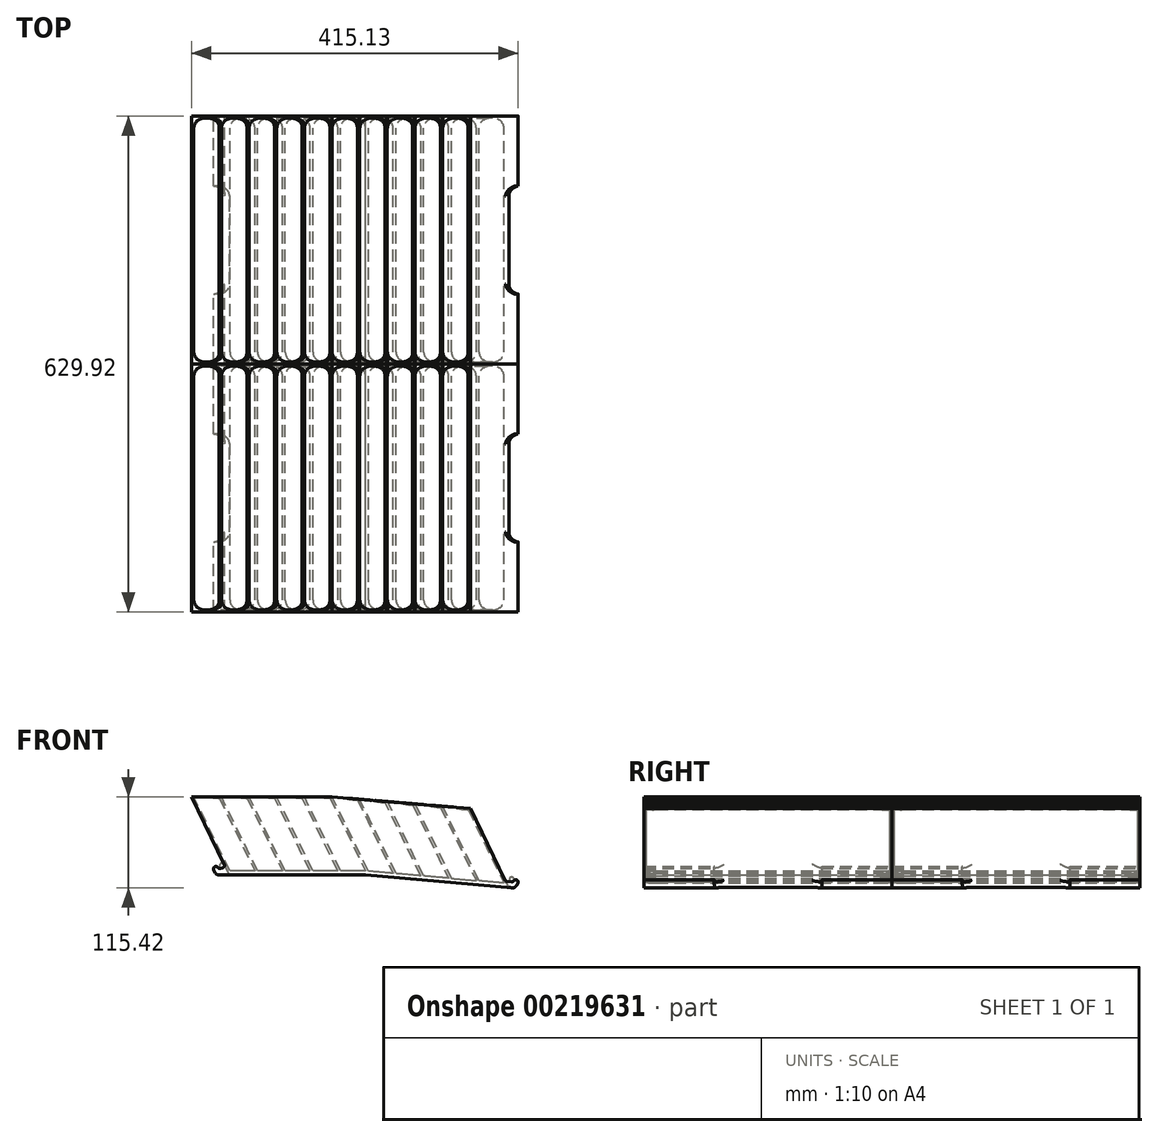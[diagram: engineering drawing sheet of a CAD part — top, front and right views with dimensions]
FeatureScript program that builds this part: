
annotation { "Feature Type Name" : "Feature", "Feature Type Description" : "" }
export const myFeature = defineFeature(function(context is Context, id is Id, definition is map)
    precondition{}
    {
        {
            var Q0;
            Q0=qCreatedBy(makeId("Front.planeOp"),FACE);
            var sketch = newSketch(context, id + "F0", { "sketchPlane" : qUnion([Q0])});
            skLineSegment(sketch, "E0", {"start": v(0, 0) * mm, "end": v(189.48, 0) * mm});
            skLineSegment(sketch, "E1", {"start": v(189.48, 0) * mm, "end": v(379.26, -16.6) * mm});
            skLineSegment(sketch, "E2", {"start": v(367.73, -8.25) * mm, "end": v(332.9, 63.16) * mm});
            skLineSegment(sketch, "E3", {"start": v(332.9, 63.16) * mm, "end": v(330.16, 61.83) * mm, "construction": true});
            skLineSegment(sketch, "E4", {"start": v(330.16, 61.83) * mm, "end": v(365.33, -10.29) * mm});
            skLineSegment(sketch, "E5", {"start": v(11.64, 10.16) * mm, "end": v(-21.71, 78.55) * mm});
            skLineSegment(sketch, "E6", {"start": v(-21.71, 78.55) * mm, "end": v(-18.66, 78.55) * mm});
            skLineSegment(sketch, "E7", {"start": v(-18.66, 78.55) * mm, "end": v(17.17, 5.08) * mm});
            skLineSegment(sketch, "E8", {"start": v(17.17, 5.08) * mm, "end": v(48.92, 5.08) * mm});
            skLineSegment(sketch, "E9", {"start": v(48.92, 5.08) * mm, "end": v(13.74, 77.21) * mm});
            skLineSegment(sketch, "E10", {"start": v(13.74, 77.21) * mm, "end": v(16.48, 78.55) * mm});
            skLineSegment(sketch, "E11", {"start": v(16.48, 78.55) * mm, "end": v(52.31, 5.08) * mm});
            skLineSegment(sketch, "E12", {"start": v(52.31, 5.08) * mm, "end": v(84.06, 5.08) * mm});
            skLineSegment(sketch, "E13", {"start": v(84.06, 5.08) * mm, "end": v(48.88, 77.21) * mm});
            skLineSegment(sketch, "E14", {"start": v(48.88, 77.21) * mm, "end": v(51.62, 78.55) * mm, "construction": true});
            skLineSegment(sketch, "E15", {"start": v(51.62, 78.55) * mm, "end": v(87.45, 5.08) * mm});
            skLineSegment(sketch, "E16", {"start": v(87.45, 5.08) * mm, "end": v(119.2, 5.08) * mm});
            skLineSegment(sketch, "E17", {"start": v(119.2, 5.08) * mm, "end": v(84.02, 77.21) * mm});
            skLineSegment(sketch, "E18", {"start": v(86.76, 78.55) * mm, "end": v(122.6, 5.08) * mm});
            skLineSegment(sketch, "E19", {"start": v(122.6, 5.08) * mm, "end": v(154.34, 5.08) * mm});
            skLineSegment(sketch, "E20", {"start": v(154.34, 5.08) * mm, "end": v(119.16, 77.21) * mm});
            skLineSegment(sketch, "E21", {"start": v(119.16, 77.21) * mm, "end": v(121.9, 78.55) * mm, "construction": true});
            skLineSegment(sketch, "E22", {"start": v(121.9, 78.55) * mm, "end": v(157.73, 5.08) * mm});
            skLineSegment(sketch, "E23", {"start": v(157.73, 5.08) * mm, "end": v(189.48, 5.08) * mm});
            skLineSegment(sketch, "E24", {"start": v(189.48, 0) * mm, "end": v(189.48, 5.08) * mm, "construction": true});
            skLineSegment(sketch, "E25", {"start": v(189.48, 5.08) * mm, "end": v(154.3, 77.21) * mm});
            skLineSegment(sketch, "E26", {"start": v(154.3, 77.21) * mm, "end": v(157.04, 78.55) * mm, "construction": true});
            skLineSegment(sketch, "E27", {"start": v(157.04, 78.55) * mm, "end": v(193.02, 4.8) * mm});
            skLineSegment(sketch, "E28", {"start": v(193.02, 4.8) * mm, "end": v(224.65, 2.02) * mm});
            skLineSegment(sketch, "E29", {"start": v(224.65, 2.02) * mm, "end": v(189.47, 74.14) * mm});
            skLineSegment(sketch, "E30", {"start": v(189.47, 74.14) * mm, "end": v(192.21, 75.47) * mm, "construction": true});
            skLineSegment(sketch, "E31", {"start": v(192.21, 75.47) * mm, "end": v(228.19, 1.71) * mm});
            skLineSegment(sketch, "E32", {"start": v(224.65, 2.02) * mm, "end": v(228.19, 1.71) * mm, "construction": true});
            skLineSegment(sketch, "E33", {"start": v(228.19, 1.71) * mm, "end": v(259.82, -1.05) * mm});
            skLineSegment(sketch, "E34", {"start": v(259.82, -1.05) * mm, "end": v(224.65, 71.06) * mm});
            skLineSegment(sketch, "E35", {"start": v(224.65, 71.06) * mm, "end": v(227.39, 72.4) * mm, "construction": true});
            skLineSegment(sketch, "E36", {"start": v(227.39, 72.4) * mm, "end": v(263.36, -1.36) * mm});
            skLineSegment(sketch, "E37", {"start": v(263.36, -1.36) * mm, "end": v(294.99, -4.13) * mm});
            skLineSegment(sketch, "E38", {"start": v(294.99, -4.13) * mm, "end": v(259.82, 67.98) * mm});
            skLineSegment(sketch, "E39", {"start": v(259.82, 67.98) * mm, "end": v(262.56, 69.32) * mm, "construction": true});
            skLineSegment(sketch, "E40", {"start": v(262.56, 69.32) * mm, "end": v(298.53, -4.44) * mm});
            skLineSegment(sketch, "E41", {"start": v(298.53, -4.44) * mm, "end": v(330.16, -7.2) * mm});
            skLineSegment(sketch, "E42", {"start": v(330.16, -7.2) * mm, "end": v(294.99, 64.9) * mm});
            skLineSegment(sketch, "E43", {"start": v(294.99, 64.9) * mm, "end": v(297.73, 66.24) * mm, "construction": true});
            skLineSegment(sketch, "E44", {"start": v(297.73, 66.24) * mm, "end": v(333.7, -7.52) * mm});
            skLineSegment(sketch, "E45", {"start": v(333.7, -7.52) * mm, "end": v(365.33, -10.29) * mm});
            skLineSegment(sketch, "E46", {"start": v(-18.66, 78.55) * mm, "end": v(157.04, 78.55) * mm, "construction": true});
            skLineSegment(sketch, "E47", {"start": v(157.04, 78.55) * mm, "end": v(332.9, 63.16) * mm, "construction": true});
            skLineSegment(sketch, "E48", {"start": v(84.02, 77.21) * mm, "end": v(86.76, 78.55) * mm, "construction": true});
            skLineSegment(sketch, "E49", {"start": v(367.73, -8.25) * mm, "end": v(376.94, -9.06) * mm});
            skLineSegment(sketch, "E50", {"start": v(379.26, -16.6) * mm, "end": v(383.77, -9.65) * mm});
            skArc(sketch, "E51", {"start": v(383.77, -9.65) * mm, "mid": v(380.63, -6.27) * mm, "end": v(376.94, -9.06) * mm});
            skLineSegment(sketch, "E52", {"start": v(376.94, -9.06) * mm, "end": v(383.77, -9.65) * mm, "construction": true});
            skLineSegment(sketch, "E53", {"start": v(0, 0) * mm, "end": v(-4.05, 7.62) * mm});
            skLineSegment(sketch, "E54", {"start": v(11.64, 10.16) * mm, "end": v(2.8, 7.62) * mm});
            skArc(sketch, "E55", {"start": v(2.8, 7.62) * mm, "mid": v(-0.62, 10.67) * mm, "end": v(-4.05, 7.62) * mm});
            skLineSegment(sketch, "E56", {"start": v(-4.05, 7.62) * mm, "end": v(2.8, 7.62) * mm, "construction": true});
            skLineSegment(sketch, "E57", {"start": v(-21.71, 78.55) * mm, "end": v(-31.72, 99.06) * mm});
            skLineSegment(sketch, "E58", {"start": v(-31.72, 99.06) * mm, "end": v(-28.67, 99.06) * mm});
            skLineSegment(sketch, "E59", {"start": v(-28.67, 99.06) * mm, "end": v(-18.66, 78.55) * mm});
            skLineSegment(sketch, "E60", {"start": v(13.74, 77.21) * mm, "end": v(3.73, 97.72) * mm});
            skLineSegment(sketch, "E61", {"start": v(3.73, 97.72) * mm, "end": v(6.47, 99.06) * mm});
            skLineSegment(sketch, "E62", {"start": v(6.47, 99.06) * mm, "end": v(16.48, 78.55) * mm});
            skLineSegment(sketch, "E63", {"start": v(48.88, 77.21) * mm, "end": v(38.87, 97.72) * mm});
            skLineSegment(sketch, "E64", {"start": v(38.87, 97.72) * mm, "end": v(41.61, 99.06) * mm});
            skLineSegment(sketch, "E65", {"start": v(41.61, 99.06) * mm, "end": v(51.62, 78.55) * mm});
            skLineSegment(sketch, "E66", {"start": v(109.16, 97.72) * mm, "end": v(111.9, 99.06) * mm});
            skLineSegment(sketch, "E67", {"start": v(259.82, 67.98) * mm, "end": v(249.49, 89.16) * mm});
            skLineSegment(sketch, "E68", {"start": v(249.49, 89.16) * mm, "end": v(252.23, 90.5) * mm});
            skLineSegment(sketch, "E69", {"start": v(252.23, 90.5) * mm, "end": v(262.56, 69.32) * mm});
            skLineSegment(sketch, "E70", {"start": v(330.16, 61.83) * mm, "end": v(319.83, 83) * mm});
            skLineSegment(sketch, "E71", {"start": v(319.83, 83) * mm, "end": v(322.57, 84.34) * mm});
            skLineSegment(sketch, "E72", {"start": v(322.57, 84.34) * mm, "end": v(332.9, 63.16) * mm});
            skLineSegment(sketch, "E73", {"start": v(154.3, 77.21) * mm, "end": v(144.3, 97.72) * mm});
            skLineSegment(sketch, "E74", {"start": v(294.99, 64.9) * mm, "end": v(284.66, 86.08) * mm});
            skLineSegment(sketch, "E75", {"start": v(189.47, 74.14) * mm, "end": v(179.15, 95.31) * mm});
            skLineSegment(sketch, "E76", {"start": v(-28.67, 99.06) * mm, "end": v(154.3, 99.06) * mm, "construction": true});
            skLineSegment(sketch, "E77", {"start": v(322.57, 84.34) * mm, "end": v(154.3, 99.06) * mm, "construction": true});
            skLineSegment(sketch, "E78", {"start": v(86.76, 78.55) * mm, "end": v(76.76, 99.06) * mm});
            skLineSegment(sketch, "E79", {"start": v(76.76, 99.06) * mm, "end": v(74.02, 97.72) * mm});
            skLineSegment(sketch, "E80", {"start": v(74.02, 97.72) * mm, "end": v(84.02, 77.21) * mm});
            skLineSegment(sketch, "E81", {"start": v(109.16, 97.72) * mm, "end": v(119.16, 77.21) * mm});
            skLineSegment(sketch, "E82", {"start": v(111.9, 99.06) * mm, "end": v(121.9, 78.55) * mm});
            skLineSegment(sketch, "E83", {"start": v(157.04, 78.55) * mm, "end": v(147.04, 99.06) * mm});
            skLineSegment(sketch, "E84", {"start": v(147.04, 99.06) * mm, "end": v(144.3, 97.72) * mm});
            skLineSegment(sketch, "E85", {"start": v(192.21, 75.47) * mm, "end": v(181.89, 96.65) * mm});
            skLineSegment(sketch, "E86", {"start": v(181.89, 96.65) * mm, "end": v(179.15, 95.31) * mm});
            skLineSegment(sketch, "E87", {"start": v(227.39, 72.4) * mm, "end": v(217.06, 93.57) * mm});
            skLineSegment(sketch, "E88", {"start": v(217.06, 93.57) * mm, "end": v(214.32, 92.23) * mm});
            skLineSegment(sketch, "E89", {"start": v(214.32, 92.23) * mm, "end": v(224.65, 71.06) * mm});
            skLineSegment(sketch, "E90", {"start": v(297.73, 66.24) * mm, "end": v(287.4, 87.42) * mm});
            skLineSegment(sketch, "E91", {"start": v(287.4, 87.42) * mm, "end": v(284.66, 86.08) * mm});
            skSolve(sketch);
        }
        {
            var Q0;
            Q0=qSketchRegion(id+"F0",true);
            extrude(context, id + "F1", {"entities" : qUnion([Q0]), "endBound" : BoundingType.SYMMETRIC, "depth" : 314.96 * mm});
        }
        {
            var Q0;
            Q0=makeQuery(id+"F1.opExtrude","SWEPT_EDGE",EDGE,{"disambiguationData":[OSD([sQuery(id+"F0.wireOp",EDGE,"E5"),sQuery(id+"F0.wireOp",EDGE,"E54")])]});
            var Q1;
            Q1=makeQuery(id+"F1.opExtrude","SWEPT_EDGE",EDGE,{"disambiguationData":[OSD([sQuery(id+"F0.wireOp",EDGE,"E54"),sQuery(id+"F0.wireOp",EDGE,"E55")])]});
            var Q2;
            Q2=makeQuery(id+"F1.opExtrude","SWEPT_EDGE",EDGE,{"disambiguationData":[OSD([sQuery(id+"F0.wireOp",EDGE,"E2"),sQuery(id+"F0.wireOp",EDGE,"E49")])]});
            var Q3;
            Q3=makeQuery(id+"F1.opExtrude","SWEPT_EDGE",EDGE,{"disambiguationData":[OSD([sQuery(id+"F0.wireOp",EDGE,"E49"),sQuery(id+"F0.wireOp",EDGE,"E51")])]});
            var Q4;
            Q4=makeQuery(id+"F1.opExtrude","SWEPT_EDGE",EDGE,{"disambiguationData":[OSD([sQuery(id+"F0.wireOp",EDGE,"E50"),sQuery(id+"F0.wireOp",EDGE,"E51")])]});
            var Q5;
            Q5=makeQuery(id+"F1.opExtrude","SWEPT_EDGE",EDGE,{"disambiguationData":[OSD([sQuery(id+"F0.wireOp",EDGE,"E53"),sQuery(id+"F0.wireOp",EDGE,"E55")])]});
            fillet(context, id + "F2", {"entities" : qUnion([Q0, Q1, Q2, Q3, Q4, Q5]), "radius" : 3.05 * mm, "tangentPropagation" : true, "allowEdgeOverflow" : false});
        }
        {
            var Q0;
            Q0=makeQuery(id+"F1.opExtrude","SWEPT_EDGE",EDGE,{"disambiguationData":[OSD([sQuery(id+"F0.wireOp",EDGE,"E0"),sQuery(id+"F0.wireOp",EDGE,"E53")])]});
            var Q1;
            Q1=makeQuery(id+"F1.opExtrude","SWEPT_EDGE",EDGE,{"disambiguationData":[OSD([sQuery(id+"F0.wireOp",EDGE,"E1"),sQuery(id+"F0.wireOp",EDGE,"E50")])]});
            fillet(context, id + "F3", {"entities" : qUnion([Q0, Q1]), "radius" : 5.08 * mm, "tangentPropagation" : true, "allowEdgeOverflow" : false});
        }
        {
            var Q0;
            Q0=makeQuery(id+"F1.opExtrude","CAP_FACE",FACE,{"disambiguationData":[OSD([sQuery(id+"F0.wireOp",EDGE,"E0"),sQuery(id+"F0.wireOp",EDGE,"E1"),sQuery(id+"F0.wireOp",EDGE,"E2"),sQuery(id+"F0.wireOp",EDGE,"E3"),sQuery(id+"F0.wireOp",EDGE,"E4"),sQuery(id+"F0.wireOp",EDGE,"E5"),sQuery(id+"F0.wireOp",EDGE,"E6"),sQuery(id+"F0.wireOp",EDGE,"E7"),sQuery(id+"F0.wireOp",EDGE,"E8"),sQuery(id+"F0.wireOp",EDGE,"E9"),sQuery(id+"F0.wireOp",EDGE,"E10"),sQuery(id+"F0.wireOp",EDGE,"E11"),sQuery(id+"F0.wireOp",EDGE,"E12"),sQuery(id+"F0.wireOp",EDGE,"E13"),sQuery(id+"F0.wireOp",EDGE,"E14"),sQuery(id+"F0.wireOp",EDGE,"E15"),sQuery(id+"F0.wireOp",EDGE,"E16"),sQuery(id+"F0.wireOp",EDGE,"E17"),sQuery(id+"F0.wireOp",EDGE,"E18"),sQuery(id+"F0.wireOp",EDGE,"E19"),sQuery(id+"F0.wireOp",EDGE,"E20"),sQuery(id+"F0.wireOp",EDGE,"E21"),sQuery(id+"F0.wireOp",EDGE,"E22"),sQuery(id+"F0.wireOp",EDGE,"E23"),sQuery(id+"F0.wireOp",EDGE,"E25"),sQuery(id+"F0.wireOp",EDGE,"E26"),sQuery(id+"F0.wireOp",EDGE,"E27"),sQuery(id+"F0.wireOp",EDGE,"E28"),sQuery(id+"F0.wireOp",EDGE,"E29"),sQuery(id+"F0.wireOp",EDGE,"E30"),sQuery(id+"F0.wireOp",EDGE,"E31"),sQuery(id+"F0.wireOp",EDGE,"E33"),sQuery(id+"F0.wireOp",EDGE,"E34"),sQuery(id+"F0.wireOp",EDGE,"E35"),sQuery(id+"F0.wireOp",EDGE,"E36"),sQuery(id+"F0.wireOp",EDGE,"E37"),sQuery(id+"F0.wireOp",EDGE,"E38"),sQuery(id+"F0.wireOp",EDGE,"E39"),sQuery(id+"F0.wireOp",EDGE,"E40"),sQuery(id+"F0.wireOp",EDGE,"E41"),sQuery(id+"F0.wireOp",EDGE,"E42"),sQuery(id+"F0.wireOp",EDGE,"E43"),sQuery(id+"F0.wireOp",EDGE,"E44"),sQuery(id+"F0.wireOp",EDGE,"E45"),sQuery(id+"F0.wireOp",EDGE,"E48"),sQuery(id+"F0.wireOp",EDGE,"E49"),sQuery(id+"F0.wireOp",EDGE,"E50"),sQuery(id+"F0.wireOp",EDGE,"E51"),sQuery(id+"F0.wireOp",EDGE,"E53"),sQuery(id+"F0.wireOp",EDGE,"E54"),sQuery(id+"F0.wireOp",EDGE,"E55")])],"isStart":false});
            var sketch = newSketch(context, id + "F4", { "sketchPlane" : qUnion([Q0])});
            skLineSegment(sketch, "E92.0", {"start": v(10.05, 13.42) * mm, "end": v(-31.72, 99.06) * mm});
            skArc(sketch, "E92.1", {"start": v(10.05, 13.42) * mm, "mid": v(10.1, 10.85) * mm, "end": v(8.15, 9.16) * mm});
            skLineSegment(sketch, "E92.2", {"start": v(8.15, 9.16) * mm, "end": v(5.3, 8.34) * mm});
            skArc(sketch, "E92.3", {"start": v(5.3, 8.34) * mm, "mid": v(3.53, 8.36) * mm, "end": v(2.08, 9.37) * mm});
            skArc(sketch, "E92.4", {"start": v(2.08, 9.37) * mm, "mid": v(0.97, 10.28) * mm, "end": v(-0.42, 10.66) * mm});
            skArc(sketch, "E92.5", {"start": v(-0.42, 10.66) * mm, "mid": v(-3.17, 9.26) * mm, "end": v(-3.3, 6.19) * mm});
            skLineSegment(sketch, "E92.6", {"start": v(-1.43, 2.7) * mm, "end": v(-3.3, 6.19) * mm});
            skArc(sketch, "E92.7", {"start": v(-1.43, 2.7) * mm, "mid": v(0.44, 0.73) * mm, "end": v(3.05, 0) * mm});
            skLineSegment(sketch, "E92.8", {"start": v(3.05, 0) * mm, "end": v(189.48, 0) * mm});
            skLineSegment(sketch, "E92.9", {"start": v(189.48, 0) * mm, "end": v(376.22, -16.34) * mm});
            skLineSegment(sketch, "E92.10", {"start": v(366.98, -6.7) * mm, "end": v(322.57, 84.34) * mm});
            skArc(sketch, "E92.11", {"start": v(369.45, -8.4) * mm, "mid": v(367.99, -7.88) * mm, "end": v(366.98, -6.7) * mm});
            skLineSegment(sketch, "E92.12", {"start": v(369.45, -8.4) * mm, "end": v(374.84, -8.87) * mm});
            skArc(sketch, "E92.13", {"start": v(377.56, -7.65) * mm, "mid": v(376.36, -8.62) * mm, "end": v(374.84, -8.87) * mm});
            skArc(sketch, "E92.14", {"start": v(380.66, -6.27) * mm, "mid": v(378.93, -6.55) * mm, "end": v(377.56, -7.65) * mm});
            skArc(sketch, "E92.15", {"start": v(382.92, -10.97) * mm, "mid": v(383.1, -7.98) * mm, "end": v(380.66, -6.27) * mm});
            skLineSegment(sketch, "E92.16", {"start": v(380.92, -14.04) * mm, "end": v(382.92, -10.97) * mm});
            skArc(sketch, "E92.17", {"start": v(376.22, -16.34) * mm, "mid": v(378.89, -15.84) * mm, "end": v(380.92, -14.04) * mm});
            skLineSegment(sketch, "E93", {"start": v(322.57, 84.34) * mm, "end": v(147.04, 99.06) * mm});
            skLineSegment(sketch, "E94", {"start": v(147.04, 99.06) * mm, "end": v(-31.72, 99.06) * mm});
            skSolve(sketch);
        }
        {
            var Q0;
            Q0=qSketchRegion(id+"F4",true);
            extrude(context, id + "F5", {"entities" : qUnion([Q0]), "oppositeDirection" : true, "depth" : 2.54 * mm});
        }
        {
            var Q0;
            Q0=makeQuery(id+"F5.opExtrude","SWEPT_BODY",BODY,{"disambiguationData":[OSD([sQuery(id+"F4.wireOp",EDGE,"E92.0"),sQuery(id+"F4.wireOp",EDGE,"E92.1"),sQuery(id+"F4.wireOp",EDGE,"E92.2"),sQuery(id+"F4.wireOp",EDGE,"E92.3"),sQuery(id+"F4.wireOp",EDGE,"E92.4"),sQuery(id+"F4.wireOp",EDGE,"E92.5"),sQuery(id+"F4.wireOp",EDGE,"E92.6"),sQuery(id+"F4.wireOp",EDGE,"E92.7"),sQuery(id+"F4.wireOp",EDGE,"E92.8"),sQuery(id+"F4.wireOp",EDGE,"E92.9"),sQuery(id+"F4.wireOp",EDGE,"E92.10"),sQuery(id+"F4.wireOp",EDGE,"E92.11"),sQuery(id+"F4.wireOp",EDGE,"E92.12"),sQuery(id+"F4.wireOp",EDGE,"E92.13"),sQuery(id+"F4.wireOp",EDGE,"E92.14"),sQuery(id+"F4.wireOp",EDGE,"E92.15"),sQuery(id+"F4.wireOp",EDGE,"E92.16"),sQuery(id+"F4.wireOp",EDGE,"E92.17"),sQuery(id+"F4.wireOp",EDGE,"E93"),sQuery(id+"F4.wireOp",EDGE,"E94")])]});
            var Q1;
            Q1=qCreatedBy(makeId("Front.planeOp"),FACE);
            mirror(context, id + "F6", {"operationType" : NewBodyOperationType.ADD, "entities" : qUnion([Q0]), "mirrorPlane" : qUnion([Q1])});
        }
        {
            var Q0;
            Q0=makeQuery(id+"F1.opExtrude","SWEPT_FACE",FACE,{"disambiguationData":[OSD([sQuery(id+"F0.wireOp",EDGE,"E61")])]});
            var sketch = newSketch(context, id + "F7", { "sketchPlane" : qUnion([Q0])});
            skLineSegment(sketch, "E95.bottom", {"start": v(14.92, -68.58) * mm, "end": v(-14.92, -68.58) * mm});
            skLineSegment(sketch, "E95.top", {"start": v(14.92, 68.58) * mm, "end": v(-14.92, 68.58) * mm});
            skLineSegment(sketch, "E95.left", {"start": v(14.92, -68.58) * mm, "end": v(14.92, 68.58) * mm});
            skLineSegment(sketch, "E95.right", {"start": v(-14.92, -68.58) * mm, "end": v(-14.92, 68.58) * mm});
            skPoint(sketch, "E95.middle", {"position": v(0, 0) * mm});
            skSolve(sketch);
        }
        {
            var Q0;
            Q0=qSketchRegion(id+"F7",true);
            extrude(context, id + "F8", {"entities" : qUnion([Q0]), "operationType" : NewBodyOperationType.REMOVE, "oppositeDirection" : true, "depth" : 144.78 * mm});
        }
        {
            var Q0;
            Q0=makeQuery(id+"F1.opExtrude","SWEPT_FACE",FACE,{"disambiguationData":[OSD([sQuery(id+"F0.wireOp",EDGE,"E61")])]});
            var sketch = newSketch(context, id + "F9", { "sketchPlane" : qUnion([Q0])});
            skLineSegment(sketch, "E96.bottom", {"start": v(326.9, -68.58) * mm, "end": v(466.95, -68.58) * mm});
            skLineSegment(sketch, "E96.top", {"start": v(326.9, 68.58) * mm, "end": v(466.95, 68.58) * mm});
            skLineSegment(sketch, "E96.left", {"start": v(326.9, -68.58) * mm, "end": v(326.9, 68.58) * mm});
            skLineSegment(sketch, "E96.right", {"start": v(466.95, -68.58) * mm, "end": v(466.95, 68.58) * mm});
            skPoint(sketch, "E96.middle", {"position": v(396.93, 0) * mm});
            skSolve(sketch);
        }
        {
            var Q0;
            Q0=qSketchRegion(id+"F9",true);
            extrude(context, id + "F10", {"entities" : qUnion([Q0]), "operationType" : NewBodyOperationType.REMOVE, "oppositeDirection" : true, "depth" : 293.12 * mm});
        }
        {
            var Q0;
            Q0=makeQuery(id+"F10.boolean.opBoolean","COPY",EDGE,{"derivedFrom":makeQuery(id+"F10.opExtrude","SWEPT_EDGE",EDGE,{"disambiguationData":[OSD([sQuery(id+"F9.wireOp",EDGE,"E96.bottom"),sQuery(id+"F9.wireOp",EDGE,"E96.left")])]})});
            var Q1;
            Q1=makeQuery(id+"F10.boolean.opBoolean","COPY",EDGE,{"derivedFrom":makeQuery(id+"F10.opExtrude","SWEPT_EDGE",EDGE,{"disambiguationData":[OSD([sQuery(id+"F9.wireOp",EDGE,"E96.top"),sQuery(id+"F9.wireOp",EDGE,"E96.left")])]})});
            var Q2;
            Q2=makeQuery(id+"F8.boolean.opBoolean","COPY",EDGE,{"derivedFrom":makeQuery(id+"F8.opExtrude","SWEPT_EDGE",EDGE,{"disambiguationData":[OSD([sQuery(id+"F7.wireOp",EDGE,"E95.top"),sQuery(id+"F7.wireOp",EDGE,"E95.left")])]})});
            var Q3;
            Q3=makeQuery(id+"F8.boolean.opBoolean","COPY",EDGE,{"derivedFrom":makeQuery(id+"F8.opExtrude","SWEPT_EDGE",EDGE,{"disambiguationData":[OSD([sQuery(id+"F7.wireOp",EDGE,"E95.bottom"),sQuery(id+"F7.wireOp",EDGE,"E95.left")])]})});
            fillet(context, id + "F11", {"entities" : qUnion([Q0, Q1, Q2, Q3]), "radius" : 12.7 * mm, "tangentPropagation" : true, "allowEdgeOverflow" : false});
        }
        {
            var Q0;
            Q0=makeQuery(id+"F6.boolean.opBoolean","INTERSECT",EDGE,{"derivedFrom":[makeQuery(id+"F1.opExtrude","SWEPT_FACE",FACE,{"disambiguationData":[OSD([sQuery(id+"F0.wireOp",EDGE,"E29"),sQuery(id+"F0.wireOp",EDGE,"E75")])]}),makeQuery(id+"F5.opExtrude","CAP_FACE",FACE,{"disambiguationData":[OSD([sQuery(id+"F4.wireOp",EDGE,"E92.0"),sQuery(id+"F4.wireOp",EDGE,"E92.1"),sQuery(id+"F4.wireOp",EDGE,"E92.2"),sQuery(id+"F4.wireOp",EDGE,"E92.3"),sQuery(id+"F4.wireOp",EDGE,"E92.4"),sQuery(id+"F4.wireOp",EDGE,"E92.5"),sQuery(id+"F4.wireOp",EDGE,"E92.6"),sQuery(id+"F4.wireOp",EDGE,"E92.7"),sQuery(id+"F4.wireOp",EDGE,"E92.8"),sQuery(id+"F4.wireOp",EDGE,"E92.9"),sQuery(id+"F4.wireOp",EDGE,"E92.10"),sQuery(id+"F4.wireOp",EDGE,"E92.11"),sQuery(id+"F4.wireOp",EDGE,"E92.12"),sQuery(id+"F4.wireOp",EDGE,"E92.13"),sQuery(id+"F4.wireOp",EDGE,"E92.14"),sQuery(id+"F4.wireOp",EDGE,"E92.15"),sQuery(id+"F4.wireOp",EDGE,"E92.16"),sQuery(id+"F4.wireOp",EDGE,"E92.17"),sQuery(id+"F4.wireOp",EDGE,"E93"),sQuery(id+"F4.wireOp",EDGE,"E94")])],"isStart":false})]});
            var Q1;
            Q1=makeQuery(id+"F6.boolean.opBoolean","INTERSECT",EDGE,{"derivedFrom":[makeQuery(id+"F1.opExtrude","SWEPT_FACE",FACE,{"disambiguationData":[OSD([sQuery(id+"F0.wireOp",EDGE,"E27"),sQuery(id+"F0.wireOp",EDGE,"E83")])]}),makeQuery(id+"F5.opExtrude","CAP_FACE",FACE,{"disambiguationData":[OSD([sQuery(id+"F4.wireOp",EDGE,"E92.0"),sQuery(id+"F4.wireOp",EDGE,"E92.1"),sQuery(id+"F4.wireOp",EDGE,"E92.2"),sQuery(id+"F4.wireOp",EDGE,"E92.3"),sQuery(id+"F4.wireOp",EDGE,"E92.4"),sQuery(id+"F4.wireOp",EDGE,"E92.5"),sQuery(id+"F4.wireOp",EDGE,"E92.6"),sQuery(id+"F4.wireOp",EDGE,"E92.7"),sQuery(id+"F4.wireOp",EDGE,"E92.8"),sQuery(id+"F4.wireOp",EDGE,"E92.9"),sQuery(id+"F4.wireOp",EDGE,"E92.10"),sQuery(id+"F4.wireOp",EDGE,"E92.11"),sQuery(id+"F4.wireOp",EDGE,"E92.12"),sQuery(id+"F4.wireOp",EDGE,"E92.13"),sQuery(id+"F4.wireOp",EDGE,"E92.14"),sQuery(id+"F4.wireOp",EDGE,"E92.15"),sQuery(id+"F4.wireOp",EDGE,"E92.16"),sQuery(id+"F4.wireOp",EDGE,"E92.17"),sQuery(id+"F4.wireOp",EDGE,"E93"),sQuery(id+"F4.wireOp",EDGE,"E94")])],"isStart":false})]});
            var Q2;
            Q2=makeQuery(id+"F6.boolean.opBoolean","INTERSECT",EDGE,{"derivedFrom":[makeQuery(id+"F1.opExtrude","SWEPT_FACE",FACE,{"disambiguationData":[OSD([sQuery(id+"F0.wireOp",EDGE,"E25"),sQuery(id+"F0.wireOp",EDGE,"E73")])]}),makeQuery(id+"F5.opExtrude","CAP_FACE",FACE,{"disambiguationData":[OSD([sQuery(id+"F4.wireOp",EDGE,"E92.0"),sQuery(id+"F4.wireOp",EDGE,"E92.1"),sQuery(id+"F4.wireOp",EDGE,"E92.2"),sQuery(id+"F4.wireOp",EDGE,"E92.3"),sQuery(id+"F4.wireOp",EDGE,"E92.4"),sQuery(id+"F4.wireOp",EDGE,"E92.5"),sQuery(id+"F4.wireOp",EDGE,"E92.6"),sQuery(id+"F4.wireOp",EDGE,"E92.7"),sQuery(id+"F4.wireOp",EDGE,"E92.8"),sQuery(id+"F4.wireOp",EDGE,"E92.9"),sQuery(id+"F4.wireOp",EDGE,"E92.10"),sQuery(id+"F4.wireOp",EDGE,"E92.11"),sQuery(id+"F4.wireOp",EDGE,"E92.12"),sQuery(id+"F4.wireOp",EDGE,"E92.13"),sQuery(id+"F4.wireOp",EDGE,"E92.14"),sQuery(id+"F4.wireOp",EDGE,"E92.15"),sQuery(id+"F4.wireOp",EDGE,"E92.16"),sQuery(id+"F4.wireOp",EDGE,"E92.17"),sQuery(id+"F4.wireOp",EDGE,"E93"),sQuery(id+"F4.wireOp",EDGE,"E94")])],"isStart":false})]});
            var Q3;
            Q3=makeQuery(id+"F6.boolean.opBoolean","INTERSECT",EDGE,{"derivedFrom":[makeQuery(id+"F1.opExtrude","SWEPT_FACE",FACE,{"disambiguationData":[OSD([sQuery(id+"F0.wireOp",EDGE,"E22"),sQuery(id+"F0.wireOp",EDGE,"E82")])]}),makeQuery(id+"F5.opExtrude","CAP_FACE",FACE,{"disambiguationData":[OSD([sQuery(id+"F4.wireOp",EDGE,"E92.0"),sQuery(id+"F4.wireOp",EDGE,"E92.1"),sQuery(id+"F4.wireOp",EDGE,"E92.2"),sQuery(id+"F4.wireOp",EDGE,"E92.3"),sQuery(id+"F4.wireOp",EDGE,"E92.4"),sQuery(id+"F4.wireOp",EDGE,"E92.5"),sQuery(id+"F4.wireOp",EDGE,"E92.6"),sQuery(id+"F4.wireOp",EDGE,"E92.7"),sQuery(id+"F4.wireOp",EDGE,"E92.8"),sQuery(id+"F4.wireOp",EDGE,"E92.9"),sQuery(id+"F4.wireOp",EDGE,"E92.10"),sQuery(id+"F4.wireOp",EDGE,"E92.11"),sQuery(id+"F4.wireOp",EDGE,"E92.12"),sQuery(id+"F4.wireOp",EDGE,"E92.13"),sQuery(id+"F4.wireOp",EDGE,"E92.14"),sQuery(id+"F4.wireOp",EDGE,"E92.15"),sQuery(id+"F4.wireOp",EDGE,"E92.16"),sQuery(id+"F4.wireOp",EDGE,"E92.17"),sQuery(id+"F4.wireOp",EDGE,"E93"),sQuery(id+"F4.wireOp",EDGE,"E94")])],"isStart":false})]});
            var Q4;
            Q4=makeQuery(id+"F6.boolean.opBoolean","INTERSECT",EDGE,{"derivedFrom":[makeQuery(id+"F1.opExtrude","SWEPT_FACE",FACE,{"disambiguationData":[OSD([sQuery(id+"F0.wireOp",EDGE,"E20"),sQuery(id+"F0.wireOp",EDGE,"E81")])]}),makeQuery(id+"F5.opExtrude","CAP_FACE",FACE,{"disambiguationData":[OSD([sQuery(id+"F4.wireOp",EDGE,"E92.0"),sQuery(id+"F4.wireOp",EDGE,"E92.1"),sQuery(id+"F4.wireOp",EDGE,"E92.2"),sQuery(id+"F4.wireOp",EDGE,"E92.3"),sQuery(id+"F4.wireOp",EDGE,"E92.4"),sQuery(id+"F4.wireOp",EDGE,"E92.5"),sQuery(id+"F4.wireOp",EDGE,"E92.6"),sQuery(id+"F4.wireOp",EDGE,"E92.7"),sQuery(id+"F4.wireOp",EDGE,"E92.8"),sQuery(id+"F4.wireOp",EDGE,"E92.9"),sQuery(id+"F4.wireOp",EDGE,"E92.10"),sQuery(id+"F4.wireOp",EDGE,"E92.11"),sQuery(id+"F4.wireOp",EDGE,"E92.12"),sQuery(id+"F4.wireOp",EDGE,"E92.13"),sQuery(id+"F4.wireOp",EDGE,"E92.14"),sQuery(id+"F4.wireOp",EDGE,"E92.15"),sQuery(id+"F4.wireOp",EDGE,"E92.16"),sQuery(id+"F4.wireOp",EDGE,"E92.17"),sQuery(id+"F4.wireOp",EDGE,"E93"),sQuery(id+"F4.wireOp",EDGE,"E94")])],"isStart":false})]});
            var Q5;
            Q5=makeQuery(id+"F6.boolean.opBoolean","INTERSECT",EDGE,{"derivedFrom":[makeQuery(id+"F1.opExtrude","SWEPT_FACE",FACE,{"disambiguationData":[OSD([sQuery(id+"F0.wireOp",EDGE,"E18"),sQuery(id+"F0.wireOp",EDGE,"E78")])]}),makeQuery(id+"F5.opExtrude","CAP_FACE",FACE,{"disambiguationData":[OSD([sQuery(id+"F4.wireOp",EDGE,"E92.0"),sQuery(id+"F4.wireOp",EDGE,"E92.1"),sQuery(id+"F4.wireOp",EDGE,"E92.2"),sQuery(id+"F4.wireOp",EDGE,"E92.3"),sQuery(id+"F4.wireOp",EDGE,"E92.4"),sQuery(id+"F4.wireOp",EDGE,"E92.5"),sQuery(id+"F4.wireOp",EDGE,"E92.6"),sQuery(id+"F4.wireOp",EDGE,"E92.7"),sQuery(id+"F4.wireOp",EDGE,"E92.8"),sQuery(id+"F4.wireOp",EDGE,"E92.9"),sQuery(id+"F4.wireOp",EDGE,"E92.10"),sQuery(id+"F4.wireOp",EDGE,"E92.11"),sQuery(id+"F4.wireOp",EDGE,"E92.12"),sQuery(id+"F4.wireOp",EDGE,"E92.13"),sQuery(id+"F4.wireOp",EDGE,"E92.14"),sQuery(id+"F4.wireOp",EDGE,"E92.15"),sQuery(id+"F4.wireOp",EDGE,"E92.16"),sQuery(id+"F4.wireOp",EDGE,"E92.17"),sQuery(id+"F4.wireOp",EDGE,"E93"),sQuery(id+"F4.wireOp",EDGE,"E94")])],"isStart":false})]});
            var Q6;
            Q6=makeQuery(id+"F6.boolean.opBoolean","INTERSECT",EDGE,{"derivedFrom":[makeQuery(id+"F1.opExtrude","SWEPT_FACE",FACE,{"disambiguationData":[OSD([sQuery(id+"F0.wireOp",EDGE,"E17"),sQuery(id+"F0.wireOp",EDGE,"E80")])]}),makeQuery(id+"F5.opExtrude","CAP_FACE",FACE,{"disambiguationData":[OSD([sQuery(id+"F4.wireOp",EDGE,"E92.0"),sQuery(id+"F4.wireOp",EDGE,"E92.1"),sQuery(id+"F4.wireOp",EDGE,"E92.2"),sQuery(id+"F4.wireOp",EDGE,"E92.3"),sQuery(id+"F4.wireOp",EDGE,"E92.4"),sQuery(id+"F4.wireOp",EDGE,"E92.5"),sQuery(id+"F4.wireOp",EDGE,"E92.6"),sQuery(id+"F4.wireOp",EDGE,"E92.7"),sQuery(id+"F4.wireOp",EDGE,"E92.8"),sQuery(id+"F4.wireOp",EDGE,"E92.9"),sQuery(id+"F4.wireOp",EDGE,"E92.10"),sQuery(id+"F4.wireOp",EDGE,"E92.11"),sQuery(id+"F4.wireOp",EDGE,"E92.12"),sQuery(id+"F4.wireOp",EDGE,"E92.13"),sQuery(id+"F4.wireOp",EDGE,"E92.14"),sQuery(id+"F4.wireOp",EDGE,"E92.15"),sQuery(id+"F4.wireOp",EDGE,"E92.16"),sQuery(id+"F4.wireOp",EDGE,"E92.17"),sQuery(id+"F4.wireOp",EDGE,"E93"),sQuery(id+"F4.wireOp",EDGE,"E94")])],"isStart":false})]});
            var Q7;
            Q7=makeQuery(id+"F6.boolean.opBoolean","INTERSECT",EDGE,{"derivedFrom":[makeQuery(id+"F1.opExtrude","SWEPT_FACE",FACE,{"disambiguationData":[OSD([sQuery(id+"F0.wireOp",EDGE,"E15"),sQuery(id+"F0.wireOp",EDGE,"E65")])]}),makeQuery(id+"F5.opExtrude","CAP_FACE",FACE,{"disambiguationData":[OSD([sQuery(id+"F4.wireOp",EDGE,"E92.0"),sQuery(id+"F4.wireOp",EDGE,"E92.1"),sQuery(id+"F4.wireOp",EDGE,"E92.2"),sQuery(id+"F4.wireOp",EDGE,"E92.3"),sQuery(id+"F4.wireOp",EDGE,"E92.4"),sQuery(id+"F4.wireOp",EDGE,"E92.5"),sQuery(id+"F4.wireOp",EDGE,"E92.6"),sQuery(id+"F4.wireOp",EDGE,"E92.7"),sQuery(id+"F4.wireOp",EDGE,"E92.8"),sQuery(id+"F4.wireOp",EDGE,"E92.9"),sQuery(id+"F4.wireOp",EDGE,"E92.10"),sQuery(id+"F4.wireOp",EDGE,"E92.11"),sQuery(id+"F4.wireOp",EDGE,"E92.12"),sQuery(id+"F4.wireOp",EDGE,"E92.13"),sQuery(id+"F4.wireOp",EDGE,"E92.14"),sQuery(id+"F4.wireOp",EDGE,"E92.15"),sQuery(id+"F4.wireOp",EDGE,"E92.16"),sQuery(id+"F4.wireOp",EDGE,"E92.17"),sQuery(id+"F4.wireOp",EDGE,"E93"),sQuery(id+"F4.wireOp",EDGE,"E94")])],"isStart":false})]});
            var Q8;
            Q8=makeQuery(id+"F6.boolean.opBoolean","INTERSECT",EDGE,{"derivedFrom":[makeQuery(id+"F1.opExtrude","SWEPT_FACE",FACE,{"disambiguationData":[OSD([sQuery(id+"F0.wireOp",EDGE,"E13"),sQuery(id+"F0.wireOp",EDGE,"E63")])]}),makeQuery(id+"F5.opExtrude","CAP_FACE",FACE,{"disambiguationData":[OSD([sQuery(id+"F4.wireOp",EDGE,"E92.0"),sQuery(id+"F4.wireOp",EDGE,"E92.1"),sQuery(id+"F4.wireOp",EDGE,"E92.2"),sQuery(id+"F4.wireOp",EDGE,"E92.3"),sQuery(id+"F4.wireOp",EDGE,"E92.4"),sQuery(id+"F4.wireOp",EDGE,"E92.5"),sQuery(id+"F4.wireOp",EDGE,"E92.6"),sQuery(id+"F4.wireOp",EDGE,"E92.7"),sQuery(id+"F4.wireOp",EDGE,"E92.8"),sQuery(id+"F4.wireOp",EDGE,"E92.9"),sQuery(id+"F4.wireOp",EDGE,"E92.10"),sQuery(id+"F4.wireOp",EDGE,"E92.11"),sQuery(id+"F4.wireOp",EDGE,"E92.12"),sQuery(id+"F4.wireOp",EDGE,"E92.13"),sQuery(id+"F4.wireOp",EDGE,"E92.14"),sQuery(id+"F4.wireOp",EDGE,"E92.15"),sQuery(id+"F4.wireOp",EDGE,"E92.16"),sQuery(id+"F4.wireOp",EDGE,"E92.17"),sQuery(id+"F4.wireOp",EDGE,"E93"),sQuery(id+"F4.wireOp",EDGE,"E94")])],"isStart":false})]});
            var Q9;
            Q9=makeQuery(id+"F6.boolean.opBoolean","INTERSECT",EDGE,{"derivedFrom":[makeQuery(id+"F1.opExtrude","SWEPT_FACE",FACE,{"disambiguationData":[OSD([sQuery(id+"F0.wireOp",EDGE,"E11"),sQuery(id+"F0.wireOp",EDGE,"E62")])]}),makeQuery(id+"F5.opExtrude","CAP_FACE",FACE,{"disambiguationData":[OSD([sQuery(id+"F4.wireOp",EDGE,"E92.0"),sQuery(id+"F4.wireOp",EDGE,"E92.1"),sQuery(id+"F4.wireOp",EDGE,"E92.2"),sQuery(id+"F4.wireOp",EDGE,"E92.3"),sQuery(id+"F4.wireOp",EDGE,"E92.4"),sQuery(id+"F4.wireOp",EDGE,"E92.5"),sQuery(id+"F4.wireOp",EDGE,"E92.6"),sQuery(id+"F4.wireOp",EDGE,"E92.7"),sQuery(id+"F4.wireOp",EDGE,"E92.8"),sQuery(id+"F4.wireOp",EDGE,"E92.9"),sQuery(id+"F4.wireOp",EDGE,"E92.10"),sQuery(id+"F4.wireOp",EDGE,"E92.11"),sQuery(id+"F4.wireOp",EDGE,"E92.12"),sQuery(id+"F4.wireOp",EDGE,"E92.13"),sQuery(id+"F4.wireOp",EDGE,"E92.14"),sQuery(id+"F4.wireOp",EDGE,"E92.15"),sQuery(id+"F4.wireOp",EDGE,"E92.16"),sQuery(id+"F4.wireOp",EDGE,"E92.17"),sQuery(id+"F4.wireOp",EDGE,"E93"),sQuery(id+"F4.wireOp",EDGE,"E94")])],"isStart":false})]});
            var Q10;
            Q10=makeQuery(id+"F6.boolean.opBoolean","INTERSECT",EDGE,{"derivedFrom":[makeQuery(id+"F1.opExtrude","SWEPT_FACE",FACE,{"disambiguationData":[OSD([sQuery(id+"F0.wireOp",EDGE,"E7"),sQuery(id+"F0.wireOp",EDGE,"E59")])]}),makeQuery(id+"F5.opExtrude","CAP_FACE",FACE,{"disambiguationData":[OSD([sQuery(id+"F4.wireOp",EDGE,"E92.0"),sQuery(id+"F4.wireOp",EDGE,"E92.1"),sQuery(id+"F4.wireOp",EDGE,"E92.2"),sQuery(id+"F4.wireOp",EDGE,"E92.3"),sQuery(id+"F4.wireOp",EDGE,"E92.4"),sQuery(id+"F4.wireOp",EDGE,"E92.5"),sQuery(id+"F4.wireOp",EDGE,"E92.6"),sQuery(id+"F4.wireOp",EDGE,"E92.7"),sQuery(id+"F4.wireOp",EDGE,"E92.8"),sQuery(id+"F4.wireOp",EDGE,"E92.9"),sQuery(id+"F4.wireOp",EDGE,"E92.10"),sQuery(id+"F4.wireOp",EDGE,"E92.11"),sQuery(id+"F4.wireOp",EDGE,"E92.12"),sQuery(id+"F4.wireOp",EDGE,"E92.13"),sQuery(id+"F4.wireOp",EDGE,"E92.14"),sQuery(id+"F4.wireOp",EDGE,"E92.15"),sQuery(id+"F4.wireOp",EDGE,"E92.16"),sQuery(id+"F4.wireOp",EDGE,"E92.17"),sQuery(id+"F4.wireOp",EDGE,"E93"),sQuery(id+"F4.wireOp",EDGE,"E94")])],"isStart":false})]});
            var Q11;
            Q11=makeQuery(id+"F6.boolean.opBoolean","INTERSECT",EDGE,{"derivedFrom":[makeQuery(id+"F1.opExtrude","SWEPT_FACE",FACE,{"disambiguationData":[OSD([sQuery(id+"F0.wireOp",EDGE,"E9"),sQuery(id+"F0.wireOp",EDGE,"E60")])]}),makeQuery(id+"F5.opExtrude","CAP_FACE",FACE,{"disambiguationData":[OSD([sQuery(id+"F4.wireOp",EDGE,"E92.0"),sQuery(id+"F4.wireOp",EDGE,"E92.1"),sQuery(id+"F4.wireOp",EDGE,"E92.2"),sQuery(id+"F4.wireOp",EDGE,"E92.3"),sQuery(id+"F4.wireOp",EDGE,"E92.4"),sQuery(id+"F4.wireOp",EDGE,"E92.5"),sQuery(id+"F4.wireOp",EDGE,"E92.6"),sQuery(id+"F4.wireOp",EDGE,"E92.7"),sQuery(id+"F4.wireOp",EDGE,"E92.8"),sQuery(id+"F4.wireOp",EDGE,"E92.9"),sQuery(id+"F4.wireOp",EDGE,"E92.10"),sQuery(id+"F4.wireOp",EDGE,"E92.11"),sQuery(id+"F4.wireOp",EDGE,"E92.12"),sQuery(id+"F4.wireOp",EDGE,"E92.13"),sQuery(id+"F4.wireOp",EDGE,"E92.14"),sQuery(id+"F4.wireOp",EDGE,"E92.15"),sQuery(id+"F4.wireOp",EDGE,"E92.16"),sQuery(id+"F4.wireOp",EDGE,"E92.17"),sQuery(id+"F4.wireOp",EDGE,"E93"),sQuery(id+"F4.wireOp",EDGE,"E94")])],"isStart":false})]});
            var Q12;
            Q12=makeQuery(id+"F6.boolean.opBoolean","INTERSECT",EDGE,{"derivedFrom":[makeQuery(id+"F1.opExtrude","SWEPT_FACE",FACE,{"disambiguationData":[OSD([sQuery(id+"F0.wireOp",EDGE,"E31"),sQuery(id+"F0.wireOp",EDGE,"E85")])]}),makeQuery(id+"F5.opExtrude","CAP_FACE",FACE,{"disambiguationData":[OSD([sQuery(id+"F4.wireOp",EDGE,"E92.0"),sQuery(id+"F4.wireOp",EDGE,"E92.1"),sQuery(id+"F4.wireOp",EDGE,"E92.2"),sQuery(id+"F4.wireOp",EDGE,"E92.3"),sQuery(id+"F4.wireOp",EDGE,"E92.4"),sQuery(id+"F4.wireOp",EDGE,"E92.5"),sQuery(id+"F4.wireOp",EDGE,"E92.6"),sQuery(id+"F4.wireOp",EDGE,"E92.7"),sQuery(id+"F4.wireOp",EDGE,"E92.8"),sQuery(id+"F4.wireOp",EDGE,"E92.9"),sQuery(id+"F4.wireOp",EDGE,"E92.10"),sQuery(id+"F4.wireOp",EDGE,"E92.11"),sQuery(id+"F4.wireOp",EDGE,"E92.12"),sQuery(id+"F4.wireOp",EDGE,"E92.13"),sQuery(id+"F4.wireOp",EDGE,"E92.14"),sQuery(id+"F4.wireOp",EDGE,"E92.15"),sQuery(id+"F4.wireOp",EDGE,"E92.16"),sQuery(id+"F4.wireOp",EDGE,"E92.17"),sQuery(id+"F4.wireOp",EDGE,"E93"),sQuery(id+"F4.wireOp",EDGE,"E94")])],"isStart":false})]});
            var Q13;
            Q13=makeQuery(id+"F6.boolean.opBoolean","INTERSECT",EDGE,{"derivedFrom":[makeQuery(id+"F1.opExtrude","SWEPT_FACE",FACE,{"disambiguationData":[OSD([sQuery(id+"F0.wireOp",EDGE,"E34"),sQuery(id+"F0.wireOp",EDGE,"E89")])]}),makeQuery(id+"F5.opExtrude","CAP_FACE",FACE,{"disambiguationData":[OSD([sQuery(id+"F4.wireOp",EDGE,"E92.0"),sQuery(id+"F4.wireOp",EDGE,"E92.1"),sQuery(id+"F4.wireOp",EDGE,"E92.2"),sQuery(id+"F4.wireOp",EDGE,"E92.3"),sQuery(id+"F4.wireOp",EDGE,"E92.4"),sQuery(id+"F4.wireOp",EDGE,"E92.5"),sQuery(id+"F4.wireOp",EDGE,"E92.6"),sQuery(id+"F4.wireOp",EDGE,"E92.7"),sQuery(id+"F4.wireOp",EDGE,"E92.8"),sQuery(id+"F4.wireOp",EDGE,"E92.9"),sQuery(id+"F4.wireOp",EDGE,"E92.10"),sQuery(id+"F4.wireOp",EDGE,"E92.11"),sQuery(id+"F4.wireOp",EDGE,"E92.12"),sQuery(id+"F4.wireOp",EDGE,"E92.13"),sQuery(id+"F4.wireOp",EDGE,"E92.14"),sQuery(id+"F4.wireOp",EDGE,"E92.15"),sQuery(id+"F4.wireOp",EDGE,"E92.16"),sQuery(id+"F4.wireOp",EDGE,"E92.17"),sQuery(id+"F4.wireOp",EDGE,"E93"),sQuery(id+"F4.wireOp",EDGE,"E94")])],"isStart":false})]});
            var Q14;
            Q14=makeQuery(id+"F6.boolean.opBoolean","INTERSECT",EDGE,{"derivedFrom":[makeQuery(id+"F1.opExtrude","SWEPT_FACE",FACE,{"disambiguationData":[OSD([sQuery(id+"F0.wireOp",EDGE,"E36"),sQuery(id+"F0.wireOp",EDGE,"E87")])]}),makeQuery(id+"F5.opExtrude","CAP_FACE",FACE,{"disambiguationData":[OSD([sQuery(id+"F4.wireOp",EDGE,"E92.0"),sQuery(id+"F4.wireOp",EDGE,"E92.1"),sQuery(id+"F4.wireOp",EDGE,"E92.2"),sQuery(id+"F4.wireOp",EDGE,"E92.3"),sQuery(id+"F4.wireOp",EDGE,"E92.4"),sQuery(id+"F4.wireOp",EDGE,"E92.5"),sQuery(id+"F4.wireOp",EDGE,"E92.6"),sQuery(id+"F4.wireOp",EDGE,"E92.7"),sQuery(id+"F4.wireOp",EDGE,"E92.8"),sQuery(id+"F4.wireOp",EDGE,"E92.9"),sQuery(id+"F4.wireOp",EDGE,"E92.10"),sQuery(id+"F4.wireOp",EDGE,"E92.11"),sQuery(id+"F4.wireOp",EDGE,"E92.12"),sQuery(id+"F4.wireOp",EDGE,"E92.13"),sQuery(id+"F4.wireOp",EDGE,"E92.14"),sQuery(id+"F4.wireOp",EDGE,"E92.15"),sQuery(id+"F4.wireOp",EDGE,"E92.16"),sQuery(id+"F4.wireOp",EDGE,"E92.17"),sQuery(id+"F4.wireOp",EDGE,"E93"),sQuery(id+"F4.wireOp",EDGE,"E94")])],"isStart":false})]});
            var Q15;
            Q15=makeQuery(id+"F6.boolean.opBoolean","INTERSECT",EDGE,{"derivedFrom":[makeQuery(id+"F1.opExtrude","SWEPT_FACE",FACE,{"disambiguationData":[OSD([sQuery(id+"F0.wireOp",EDGE,"E38"),sQuery(id+"F0.wireOp",EDGE,"E67")])]}),makeQuery(id+"F5.opExtrude","CAP_FACE",FACE,{"disambiguationData":[OSD([sQuery(id+"F4.wireOp",EDGE,"E92.0"),sQuery(id+"F4.wireOp",EDGE,"E92.1"),sQuery(id+"F4.wireOp",EDGE,"E92.2"),sQuery(id+"F4.wireOp",EDGE,"E92.3"),sQuery(id+"F4.wireOp",EDGE,"E92.4"),sQuery(id+"F4.wireOp",EDGE,"E92.5"),sQuery(id+"F4.wireOp",EDGE,"E92.6"),sQuery(id+"F4.wireOp",EDGE,"E92.7"),sQuery(id+"F4.wireOp",EDGE,"E92.8"),sQuery(id+"F4.wireOp",EDGE,"E92.9"),sQuery(id+"F4.wireOp",EDGE,"E92.10"),sQuery(id+"F4.wireOp",EDGE,"E92.11"),sQuery(id+"F4.wireOp",EDGE,"E92.12"),sQuery(id+"F4.wireOp",EDGE,"E92.13"),sQuery(id+"F4.wireOp",EDGE,"E92.14"),sQuery(id+"F4.wireOp",EDGE,"E92.15"),sQuery(id+"F4.wireOp",EDGE,"E92.16"),sQuery(id+"F4.wireOp",EDGE,"E92.17"),sQuery(id+"F4.wireOp",EDGE,"E93"),sQuery(id+"F4.wireOp",EDGE,"E94")])],"isStart":false})]});
            var Q16;
            Q16=makeQuery(id+"F6.boolean.opBoolean","INTERSECT",EDGE,{"derivedFrom":[makeQuery(id+"F1.opExtrude","SWEPT_FACE",FACE,{"disambiguationData":[OSD([sQuery(id+"F0.wireOp",EDGE,"E42"),sQuery(id+"F0.wireOp",EDGE,"E74")])]}),makeQuery(id+"F5.opExtrude","CAP_FACE",FACE,{"disambiguationData":[OSD([sQuery(id+"F4.wireOp",EDGE,"E92.0"),sQuery(id+"F4.wireOp",EDGE,"E92.1"),sQuery(id+"F4.wireOp",EDGE,"E92.2"),sQuery(id+"F4.wireOp",EDGE,"E92.3"),sQuery(id+"F4.wireOp",EDGE,"E92.4"),sQuery(id+"F4.wireOp",EDGE,"E92.5"),sQuery(id+"F4.wireOp",EDGE,"E92.6"),sQuery(id+"F4.wireOp",EDGE,"E92.7"),sQuery(id+"F4.wireOp",EDGE,"E92.8"),sQuery(id+"F4.wireOp",EDGE,"E92.9"),sQuery(id+"F4.wireOp",EDGE,"E92.10"),sQuery(id+"F4.wireOp",EDGE,"E92.11"),sQuery(id+"F4.wireOp",EDGE,"E92.12"),sQuery(id+"F4.wireOp",EDGE,"E92.13"),sQuery(id+"F4.wireOp",EDGE,"E92.14"),sQuery(id+"F4.wireOp",EDGE,"E92.15"),sQuery(id+"F4.wireOp",EDGE,"E92.16"),sQuery(id+"F4.wireOp",EDGE,"E92.17"),sQuery(id+"F4.wireOp",EDGE,"E93"),sQuery(id+"F4.wireOp",EDGE,"E94")])],"isStart":false})]});
            var Q17;
            Q17=makeQuery(id+"F6.boolean.opBoolean","INTERSECT",EDGE,{"derivedFrom":[makeQuery(id+"F1.opExtrude","SWEPT_FACE",FACE,{"disambiguationData":[OSD([sQuery(id+"F0.wireOp",EDGE,"E4"),sQuery(id+"F0.wireOp",EDGE,"E70")])]}),makeQuery(id+"F5.opExtrude","CAP_FACE",FACE,{"disambiguationData":[OSD([sQuery(id+"F4.wireOp",EDGE,"E92.0"),sQuery(id+"F4.wireOp",EDGE,"E92.1"),sQuery(id+"F4.wireOp",EDGE,"E92.2"),sQuery(id+"F4.wireOp",EDGE,"E92.3"),sQuery(id+"F4.wireOp",EDGE,"E92.4"),sQuery(id+"F4.wireOp",EDGE,"E92.5"),sQuery(id+"F4.wireOp",EDGE,"E92.6"),sQuery(id+"F4.wireOp",EDGE,"E92.7"),sQuery(id+"F4.wireOp",EDGE,"E92.8"),sQuery(id+"F4.wireOp",EDGE,"E92.9"),sQuery(id+"F4.wireOp",EDGE,"E92.10"),sQuery(id+"F4.wireOp",EDGE,"E92.11"),sQuery(id+"F4.wireOp",EDGE,"E92.12"),sQuery(id+"F4.wireOp",EDGE,"E92.13"),sQuery(id+"F4.wireOp",EDGE,"E92.14"),sQuery(id+"F4.wireOp",EDGE,"E92.15"),sQuery(id+"F4.wireOp",EDGE,"E92.16"),sQuery(id+"F4.wireOp",EDGE,"E92.17"),sQuery(id+"F4.wireOp",EDGE,"E93"),sQuery(id+"F4.wireOp",EDGE,"E94")])],"isStart":false})]});
            var Q18;
            Q18=makeQuery(id+"F6.boolean.opBoolean","INTERSECT",EDGE,{"derivedFrom":[makeQuery(id+"F1.opExtrude","SWEPT_FACE",FACE,{"disambiguationData":[OSD([sQuery(id+"F0.wireOp",EDGE,"E44"),sQuery(id+"F0.wireOp",EDGE,"E90")])]}),makeQuery(id+"F5.opExtrude","CAP_FACE",FACE,{"disambiguationData":[OSD([sQuery(id+"F4.wireOp",EDGE,"E92.0"),sQuery(id+"F4.wireOp",EDGE,"E92.1"),sQuery(id+"F4.wireOp",EDGE,"E92.2"),sQuery(id+"F4.wireOp",EDGE,"E92.3"),sQuery(id+"F4.wireOp",EDGE,"E92.4"),sQuery(id+"F4.wireOp",EDGE,"E92.5"),sQuery(id+"F4.wireOp",EDGE,"E92.6"),sQuery(id+"F4.wireOp",EDGE,"E92.7"),sQuery(id+"F4.wireOp",EDGE,"E92.8"),sQuery(id+"F4.wireOp",EDGE,"E92.9"),sQuery(id+"F4.wireOp",EDGE,"E92.10"),sQuery(id+"F4.wireOp",EDGE,"E92.11"),sQuery(id+"F4.wireOp",EDGE,"E92.12"),sQuery(id+"F4.wireOp",EDGE,"E92.13"),sQuery(id+"F4.wireOp",EDGE,"E92.14"),sQuery(id+"F4.wireOp",EDGE,"E92.15"),sQuery(id+"F4.wireOp",EDGE,"E92.16"),sQuery(id+"F4.wireOp",EDGE,"E92.17"),sQuery(id+"F4.wireOp",EDGE,"E93"),sQuery(id+"F4.wireOp",EDGE,"E94")])],"isStart":false})]});
            var Q19;
            Q19=makeQuery(id+"F6.boolean.opBoolean","INTERSECT",EDGE,{"derivedFrom":[makeQuery(id+"F1.opExtrude","SWEPT_FACE",FACE,{"disambiguationData":[OSD([sQuery(id+"F0.wireOp",EDGE,"E44"),sQuery(id+"F0.wireOp",EDGE,"E90")])]}),makeQuery(id+"F6.opPattern","COPY",FACE,{"derivedFrom":makeQuery(id+"F5.opExtrude","CAP_FACE",FACE,{"disambiguationData":[OSD([sQuery(id+"F4.wireOp",EDGE,"E92.0"),sQuery(id+"F4.wireOp",EDGE,"E92.1"),sQuery(id+"F4.wireOp",EDGE,"E92.2"),sQuery(id+"F4.wireOp",EDGE,"E92.3"),sQuery(id+"F4.wireOp",EDGE,"E92.4"),sQuery(id+"F4.wireOp",EDGE,"E92.5"),sQuery(id+"F4.wireOp",EDGE,"E92.6"),sQuery(id+"F4.wireOp",EDGE,"E92.7"),sQuery(id+"F4.wireOp",EDGE,"E92.8"),sQuery(id+"F4.wireOp",EDGE,"E92.9"),sQuery(id+"F4.wireOp",EDGE,"E92.10"),sQuery(id+"F4.wireOp",EDGE,"E92.11"),sQuery(id+"F4.wireOp",EDGE,"E92.12"),sQuery(id+"F4.wireOp",EDGE,"E92.13"),sQuery(id+"F4.wireOp",EDGE,"E92.14"),sQuery(id+"F4.wireOp",EDGE,"E92.15"),sQuery(id+"F4.wireOp",EDGE,"E92.16"),sQuery(id+"F4.wireOp",EDGE,"E92.17"),sQuery(id+"F4.wireOp",EDGE,"E93"),sQuery(id+"F4.wireOp",EDGE,"E94")])],"isStart":false}),"instanceName":"1"})]});
            var Q20;
            Q20=makeQuery(id+"F6.boolean.opBoolean","INTERSECT",EDGE,{"derivedFrom":[makeQuery(id+"F1.opExtrude","SWEPT_FACE",FACE,{"disambiguationData":[OSD([sQuery(id+"F0.wireOp",EDGE,"E40"),sQuery(id+"F0.wireOp",EDGE,"E69")])]}),makeQuery(id+"F6.opPattern","COPY",FACE,{"derivedFrom":makeQuery(id+"F5.opExtrude","CAP_FACE",FACE,{"disambiguationData":[OSD([sQuery(id+"F4.wireOp",EDGE,"E92.0"),sQuery(id+"F4.wireOp",EDGE,"E92.1"),sQuery(id+"F4.wireOp",EDGE,"E92.2"),sQuery(id+"F4.wireOp",EDGE,"E92.3"),sQuery(id+"F4.wireOp",EDGE,"E92.4"),sQuery(id+"F4.wireOp",EDGE,"E92.5"),sQuery(id+"F4.wireOp",EDGE,"E92.6"),sQuery(id+"F4.wireOp",EDGE,"E92.7"),sQuery(id+"F4.wireOp",EDGE,"E92.8"),sQuery(id+"F4.wireOp",EDGE,"E92.9"),sQuery(id+"F4.wireOp",EDGE,"E92.10"),sQuery(id+"F4.wireOp",EDGE,"E92.11"),sQuery(id+"F4.wireOp",EDGE,"E92.12"),sQuery(id+"F4.wireOp",EDGE,"E92.13"),sQuery(id+"F4.wireOp",EDGE,"E92.14"),sQuery(id+"F4.wireOp",EDGE,"E92.15"),sQuery(id+"F4.wireOp",EDGE,"E92.16"),sQuery(id+"F4.wireOp",EDGE,"E92.17"),sQuery(id+"F4.wireOp",EDGE,"E93"),sQuery(id+"F4.wireOp",EDGE,"E94")])],"isStart":false}),"instanceName":"1"})]});
            var Q21;
            Q21=makeQuery(id+"F6.boolean.opBoolean","INTERSECT",EDGE,{"derivedFrom":[makeQuery(id+"F1.opExtrude","SWEPT_FACE",FACE,{"disambiguationData":[OSD([sQuery(id+"F0.wireOp",EDGE,"E36"),sQuery(id+"F0.wireOp",EDGE,"E87")])]}),makeQuery(id+"F6.opPattern","COPY",FACE,{"derivedFrom":makeQuery(id+"F5.opExtrude","CAP_FACE",FACE,{"disambiguationData":[OSD([sQuery(id+"F4.wireOp",EDGE,"E92.0"),sQuery(id+"F4.wireOp",EDGE,"E92.1"),sQuery(id+"F4.wireOp",EDGE,"E92.2"),sQuery(id+"F4.wireOp",EDGE,"E92.3"),sQuery(id+"F4.wireOp",EDGE,"E92.4"),sQuery(id+"F4.wireOp",EDGE,"E92.5"),sQuery(id+"F4.wireOp",EDGE,"E92.6"),sQuery(id+"F4.wireOp",EDGE,"E92.7"),sQuery(id+"F4.wireOp",EDGE,"E92.8"),sQuery(id+"F4.wireOp",EDGE,"E92.9"),sQuery(id+"F4.wireOp",EDGE,"E92.10"),sQuery(id+"F4.wireOp",EDGE,"E92.11"),sQuery(id+"F4.wireOp",EDGE,"E92.12"),sQuery(id+"F4.wireOp",EDGE,"E92.13"),sQuery(id+"F4.wireOp",EDGE,"E92.14"),sQuery(id+"F4.wireOp",EDGE,"E92.15"),sQuery(id+"F4.wireOp",EDGE,"E92.16"),sQuery(id+"F4.wireOp",EDGE,"E92.17"),sQuery(id+"F4.wireOp",EDGE,"E93"),sQuery(id+"F4.wireOp",EDGE,"E94")])],"isStart":false}),"instanceName":"1"})]});
            var Q22;
            Q22=makeQuery(id+"F6.boolean.opBoolean","INTERSECT",EDGE,{"derivedFrom":[makeQuery(id+"F1.opExtrude","SWEPT_FACE",FACE,{"disambiguationData":[OSD([sQuery(id+"F0.wireOp",EDGE,"E31"),sQuery(id+"F0.wireOp",EDGE,"E85")])]}),makeQuery(id+"F6.opPattern","COPY",FACE,{"derivedFrom":makeQuery(id+"F5.opExtrude","CAP_FACE",FACE,{"disambiguationData":[OSD([sQuery(id+"F4.wireOp",EDGE,"E92.0"),sQuery(id+"F4.wireOp",EDGE,"E92.1"),sQuery(id+"F4.wireOp",EDGE,"E92.2"),sQuery(id+"F4.wireOp",EDGE,"E92.3"),sQuery(id+"F4.wireOp",EDGE,"E92.4"),sQuery(id+"F4.wireOp",EDGE,"E92.5"),sQuery(id+"F4.wireOp",EDGE,"E92.6"),sQuery(id+"F4.wireOp",EDGE,"E92.7"),sQuery(id+"F4.wireOp",EDGE,"E92.8"),sQuery(id+"F4.wireOp",EDGE,"E92.9"),sQuery(id+"F4.wireOp",EDGE,"E92.10"),sQuery(id+"F4.wireOp",EDGE,"E92.11"),sQuery(id+"F4.wireOp",EDGE,"E92.12"),sQuery(id+"F4.wireOp",EDGE,"E92.13"),sQuery(id+"F4.wireOp",EDGE,"E92.14"),sQuery(id+"F4.wireOp",EDGE,"E92.15"),sQuery(id+"F4.wireOp",EDGE,"E92.16"),sQuery(id+"F4.wireOp",EDGE,"E92.17"),sQuery(id+"F4.wireOp",EDGE,"E93"),sQuery(id+"F4.wireOp",EDGE,"E94")])],"isStart":false}),"instanceName":"1"})]});
            var Q23;
            Q23=makeQuery(id+"F6.boolean.opBoolean","INTERSECT",EDGE,{"derivedFrom":[makeQuery(id+"F1.opExtrude","SWEPT_FACE",FACE,{"disambiguationData":[OSD([sQuery(id+"F0.wireOp",EDGE,"E27"),sQuery(id+"F0.wireOp",EDGE,"E83")])]}),makeQuery(id+"F6.opPattern","COPY",FACE,{"derivedFrom":makeQuery(id+"F5.opExtrude","CAP_FACE",FACE,{"disambiguationData":[OSD([sQuery(id+"F4.wireOp",EDGE,"E92.0"),sQuery(id+"F4.wireOp",EDGE,"E92.1"),sQuery(id+"F4.wireOp",EDGE,"E92.2"),sQuery(id+"F4.wireOp",EDGE,"E92.3"),sQuery(id+"F4.wireOp",EDGE,"E92.4"),sQuery(id+"F4.wireOp",EDGE,"E92.5"),sQuery(id+"F4.wireOp",EDGE,"E92.6"),sQuery(id+"F4.wireOp",EDGE,"E92.7"),sQuery(id+"F4.wireOp",EDGE,"E92.8"),sQuery(id+"F4.wireOp",EDGE,"E92.9"),sQuery(id+"F4.wireOp",EDGE,"E92.10"),sQuery(id+"F4.wireOp",EDGE,"E92.11"),sQuery(id+"F4.wireOp",EDGE,"E92.12"),sQuery(id+"F4.wireOp",EDGE,"E92.13"),sQuery(id+"F4.wireOp",EDGE,"E92.14"),sQuery(id+"F4.wireOp",EDGE,"E92.15"),sQuery(id+"F4.wireOp",EDGE,"E92.16"),sQuery(id+"F4.wireOp",EDGE,"E92.17"),sQuery(id+"F4.wireOp",EDGE,"E93"),sQuery(id+"F4.wireOp",EDGE,"E94")])],"isStart":false}),"instanceName":"1"})]});
            var Q24;
            Q24=makeQuery(id+"F6.boolean.opBoolean","INTERSECT",EDGE,{"derivedFrom":[makeQuery(id+"F1.opExtrude","SWEPT_FACE",FACE,{"disambiguationData":[OSD([sQuery(id+"F0.wireOp",EDGE,"E22"),sQuery(id+"F0.wireOp",EDGE,"E82")])]}),makeQuery(id+"F6.opPattern","COPY",FACE,{"derivedFrom":makeQuery(id+"F5.opExtrude","CAP_FACE",FACE,{"disambiguationData":[OSD([sQuery(id+"F4.wireOp",EDGE,"E92.0"),sQuery(id+"F4.wireOp",EDGE,"E92.1"),sQuery(id+"F4.wireOp",EDGE,"E92.2"),sQuery(id+"F4.wireOp",EDGE,"E92.3"),sQuery(id+"F4.wireOp",EDGE,"E92.4"),sQuery(id+"F4.wireOp",EDGE,"E92.5"),sQuery(id+"F4.wireOp",EDGE,"E92.6"),sQuery(id+"F4.wireOp",EDGE,"E92.7"),sQuery(id+"F4.wireOp",EDGE,"E92.8"),sQuery(id+"F4.wireOp",EDGE,"E92.9"),sQuery(id+"F4.wireOp",EDGE,"E92.10"),sQuery(id+"F4.wireOp",EDGE,"E92.11"),sQuery(id+"F4.wireOp",EDGE,"E92.12"),sQuery(id+"F4.wireOp",EDGE,"E92.13"),sQuery(id+"F4.wireOp",EDGE,"E92.14"),sQuery(id+"F4.wireOp",EDGE,"E92.15"),sQuery(id+"F4.wireOp",EDGE,"E92.16"),sQuery(id+"F4.wireOp",EDGE,"E92.17"),sQuery(id+"F4.wireOp",EDGE,"E93"),sQuery(id+"F4.wireOp",EDGE,"E94")])],"isStart":false}),"instanceName":"1"})]});
            var Q25;
            Q25=makeQuery(id+"F6.boolean.opBoolean","INTERSECT",EDGE,{"derivedFrom":[makeQuery(id+"F1.opExtrude","SWEPT_FACE",FACE,{"disambiguationData":[OSD([sQuery(id+"F0.wireOp",EDGE,"E18"),sQuery(id+"F0.wireOp",EDGE,"E78")])]}),makeQuery(id+"F6.opPattern","COPY",FACE,{"derivedFrom":makeQuery(id+"F5.opExtrude","CAP_FACE",FACE,{"disambiguationData":[OSD([sQuery(id+"F4.wireOp",EDGE,"E92.0"),sQuery(id+"F4.wireOp",EDGE,"E92.1"),sQuery(id+"F4.wireOp",EDGE,"E92.2"),sQuery(id+"F4.wireOp",EDGE,"E92.3"),sQuery(id+"F4.wireOp",EDGE,"E92.4"),sQuery(id+"F4.wireOp",EDGE,"E92.5"),sQuery(id+"F4.wireOp",EDGE,"E92.6"),sQuery(id+"F4.wireOp",EDGE,"E92.7"),sQuery(id+"F4.wireOp",EDGE,"E92.8"),sQuery(id+"F4.wireOp",EDGE,"E92.9"),sQuery(id+"F4.wireOp",EDGE,"E92.10"),sQuery(id+"F4.wireOp",EDGE,"E92.11"),sQuery(id+"F4.wireOp",EDGE,"E92.12"),sQuery(id+"F4.wireOp",EDGE,"E92.13"),sQuery(id+"F4.wireOp",EDGE,"E92.14"),sQuery(id+"F4.wireOp",EDGE,"E92.15"),sQuery(id+"F4.wireOp",EDGE,"E92.16"),sQuery(id+"F4.wireOp",EDGE,"E92.17"),sQuery(id+"F4.wireOp",EDGE,"E93"),sQuery(id+"F4.wireOp",EDGE,"E94")])],"isStart":false}),"instanceName":"1"})]});
            var Q26;
            Q26=makeQuery(id+"F6.boolean.opBoolean","INTERSECT",EDGE,{"derivedFrom":[makeQuery(id+"F1.opExtrude","SWEPT_FACE",FACE,{"disambiguationData":[OSD([sQuery(id+"F0.wireOp",EDGE,"E15"),sQuery(id+"F0.wireOp",EDGE,"E65")])]}),makeQuery(id+"F6.opPattern","COPY",FACE,{"derivedFrom":makeQuery(id+"F5.opExtrude","CAP_FACE",FACE,{"disambiguationData":[OSD([sQuery(id+"F4.wireOp",EDGE,"E92.0"),sQuery(id+"F4.wireOp",EDGE,"E92.1"),sQuery(id+"F4.wireOp",EDGE,"E92.2"),sQuery(id+"F4.wireOp",EDGE,"E92.3"),sQuery(id+"F4.wireOp",EDGE,"E92.4"),sQuery(id+"F4.wireOp",EDGE,"E92.5"),sQuery(id+"F4.wireOp",EDGE,"E92.6"),sQuery(id+"F4.wireOp",EDGE,"E92.7"),sQuery(id+"F4.wireOp",EDGE,"E92.8"),sQuery(id+"F4.wireOp",EDGE,"E92.9"),sQuery(id+"F4.wireOp",EDGE,"E92.10"),sQuery(id+"F4.wireOp",EDGE,"E92.11"),sQuery(id+"F4.wireOp",EDGE,"E92.12"),sQuery(id+"F4.wireOp",EDGE,"E92.13"),sQuery(id+"F4.wireOp",EDGE,"E92.14"),sQuery(id+"F4.wireOp",EDGE,"E92.15"),sQuery(id+"F4.wireOp",EDGE,"E92.16"),sQuery(id+"F4.wireOp",EDGE,"E92.17"),sQuery(id+"F4.wireOp",EDGE,"E93"),sQuery(id+"F4.wireOp",EDGE,"E94")])],"isStart":false}),"instanceName":"1"})]});
            var Q27;
            Q27=makeQuery(id+"F6.boolean.opBoolean","INTERSECT",EDGE,{"derivedFrom":[makeQuery(id+"F1.opExtrude","SWEPT_FACE",FACE,{"disambiguationData":[OSD([sQuery(id+"F0.wireOp",EDGE,"E11"),sQuery(id+"F0.wireOp",EDGE,"E62")])]}),makeQuery(id+"F6.opPattern","COPY",FACE,{"derivedFrom":makeQuery(id+"F5.opExtrude","CAP_FACE",FACE,{"disambiguationData":[OSD([sQuery(id+"F4.wireOp",EDGE,"E92.0"),sQuery(id+"F4.wireOp",EDGE,"E92.1"),sQuery(id+"F4.wireOp",EDGE,"E92.2"),sQuery(id+"F4.wireOp",EDGE,"E92.3"),sQuery(id+"F4.wireOp",EDGE,"E92.4"),sQuery(id+"F4.wireOp",EDGE,"E92.5"),sQuery(id+"F4.wireOp",EDGE,"E92.6"),sQuery(id+"F4.wireOp",EDGE,"E92.7"),sQuery(id+"F4.wireOp",EDGE,"E92.8"),sQuery(id+"F4.wireOp",EDGE,"E92.9"),sQuery(id+"F4.wireOp",EDGE,"E92.10"),sQuery(id+"F4.wireOp",EDGE,"E92.11"),sQuery(id+"F4.wireOp",EDGE,"E92.12"),sQuery(id+"F4.wireOp",EDGE,"E92.13"),sQuery(id+"F4.wireOp",EDGE,"E92.14"),sQuery(id+"F4.wireOp",EDGE,"E92.15"),sQuery(id+"F4.wireOp",EDGE,"E92.16"),sQuery(id+"F4.wireOp",EDGE,"E92.17"),sQuery(id+"F4.wireOp",EDGE,"E93"),sQuery(id+"F4.wireOp",EDGE,"E94")])],"isStart":false}),"instanceName":"1"})]});
            var Q28;
            Q28=makeQuery(id+"F6.boolean.opBoolean","INTERSECT",EDGE,{"derivedFrom":[makeQuery(id+"F1.opExtrude","SWEPT_FACE",FACE,{"disambiguationData":[OSD([sQuery(id+"F0.wireOp",EDGE,"E7"),sQuery(id+"F0.wireOp",EDGE,"E59")])]}),makeQuery(id+"F6.opPattern","COPY",FACE,{"derivedFrom":makeQuery(id+"F5.opExtrude","CAP_FACE",FACE,{"disambiguationData":[OSD([sQuery(id+"F4.wireOp",EDGE,"E92.0"),sQuery(id+"F4.wireOp",EDGE,"E92.1"),sQuery(id+"F4.wireOp",EDGE,"E92.2"),sQuery(id+"F4.wireOp",EDGE,"E92.3"),sQuery(id+"F4.wireOp",EDGE,"E92.4"),sQuery(id+"F4.wireOp",EDGE,"E92.5"),sQuery(id+"F4.wireOp",EDGE,"E92.6"),sQuery(id+"F4.wireOp",EDGE,"E92.7"),sQuery(id+"F4.wireOp",EDGE,"E92.8"),sQuery(id+"F4.wireOp",EDGE,"E92.9"),sQuery(id+"F4.wireOp",EDGE,"E92.10"),sQuery(id+"F4.wireOp",EDGE,"E92.11"),sQuery(id+"F4.wireOp",EDGE,"E92.12"),sQuery(id+"F4.wireOp",EDGE,"E92.13"),sQuery(id+"F4.wireOp",EDGE,"E92.14"),sQuery(id+"F4.wireOp",EDGE,"E92.15"),sQuery(id+"F4.wireOp",EDGE,"E92.16"),sQuery(id+"F4.wireOp",EDGE,"E92.17"),sQuery(id+"F4.wireOp",EDGE,"E93"),sQuery(id+"F4.wireOp",EDGE,"E94")])],"isStart":false}),"instanceName":"1"})]});
            var Q29;
            Q29=makeQuery(id+"F6.boolean.opBoolean","INTERSECT",EDGE,{"derivedFrom":[makeQuery(id+"F1.opExtrude","SWEPT_FACE",FACE,{"disambiguationData":[OSD([sQuery(id+"F0.wireOp",EDGE,"E4"),sQuery(id+"F0.wireOp",EDGE,"E70")])]}),makeQuery(id+"F6.opPattern","COPY",FACE,{"derivedFrom":makeQuery(id+"F5.opExtrude","CAP_FACE",FACE,{"disambiguationData":[OSD([sQuery(id+"F4.wireOp",EDGE,"E92.0"),sQuery(id+"F4.wireOp",EDGE,"E92.1"),sQuery(id+"F4.wireOp",EDGE,"E92.2"),sQuery(id+"F4.wireOp",EDGE,"E92.3"),sQuery(id+"F4.wireOp",EDGE,"E92.4"),sQuery(id+"F4.wireOp",EDGE,"E92.5"),sQuery(id+"F4.wireOp",EDGE,"E92.6"),sQuery(id+"F4.wireOp",EDGE,"E92.7"),sQuery(id+"F4.wireOp",EDGE,"E92.8"),sQuery(id+"F4.wireOp",EDGE,"E92.9"),sQuery(id+"F4.wireOp",EDGE,"E92.10"),sQuery(id+"F4.wireOp",EDGE,"E92.11"),sQuery(id+"F4.wireOp",EDGE,"E92.12"),sQuery(id+"F4.wireOp",EDGE,"E92.13"),sQuery(id+"F4.wireOp",EDGE,"E92.14"),sQuery(id+"F4.wireOp",EDGE,"E92.15"),sQuery(id+"F4.wireOp",EDGE,"E92.16"),sQuery(id+"F4.wireOp",EDGE,"E92.17"),sQuery(id+"F4.wireOp",EDGE,"E93"),sQuery(id+"F4.wireOp",EDGE,"E94")])],"isStart":false}),"instanceName":"1"})]});
            var Q30;
            Q30=makeQuery(id+"F6.boolean.opBoolean","INTERSECT",EDGE,{"derivedFrom":[makeQuery(id+"F1.opExtrude","SWEPT_FACE",FACE,{"disambiguationData":[OSD([sQuery(id+"F0.wireOp",EDGE,"E42"),sQuery(id+"F0.wireOp",EDGE,"E74")])]}),makeQuery(id+"F6.opPattern","COPY",FACE,{"derivedFrom":makeQuery(id+"F5.opExtrude","CAP_FACE",FACE,{"disambiguationData":[OSD([sQuery(id+"F4.wireOp",EDGE,"E92.0"),sQuery(id+"F4.wireOp",EDGE,"E92.1"),sQuery(id+"F4.wireOp",EDGE,"E92.2"),sQuery(id+"F4.wireOp",EDGE,"E92.3"),sQuery(id+"F4.wireOp",EDGE,"E92.4"),sQuery(id+"F4.wireOp",EDGE,"E92.5"),sQuery(id+"F4.wireOp",EDGE,"E92.6"),sQuery(id+"F4.wireOp",EDGE,"E92.7"),sQuery(id+"F4.wireOp",EDGE,"E92.8"),sQuery(id+"F4.wireOp",EDGE,"E92.9"),sQuery(id+"F4.wireOp",EDGE,"E92.10"),sQuery(id+"F4.wireOp",EDGE,"E92.11"),sQuery(id+"F4.wireOp",EDGE,"E92.12"),sQuery(id+"F4.wireOp",EDGE,"E92.13"),sQuery(id+"F4.wireOp",EDGE,"E92.14"),sQuery(id+"F4.wireOp",EDGE,"E92.15"),sQuery(id+"F4.wireOp",EDGE,"E92.16"),sQuery(id+"F4.wireOp",EDGE,"E92.17"),sQuery(id+"F4.wireOp",EDGE,"E93"),sQuery(id+"F4.wireOp",EDGE,"E94")])],"isStart":false}),"instanceName":"1"})]});
            var Q31;
            Q31=makeQuery(id+"F6.boolean.opBoolean","INTERSECT",EDGE,{"derivedFrom":[makeQuery(id+"F1.opExtrude","SWEPT_FACE",FACE,{"disambiguationData":[OSD([sQuery(id+"F0.wireOp",EDGE,"E38"),sQuery(id+"F0.wireOp",EDGE,"E67")])]}),makeQuery(id+"F6.opPattern","COPY",FACE,{"derivedFrom":makeQuery(id+"F5.opExtrude","CAP_FACE",FACE,{"disambiguationData":[OSD([sQuery(id+"F4.wireOp",EDGE,"E92.0"),sQuery(id+"F4.wireOp",EDGE,"E92.1"),sQuery(id+"F4.wireOp",EDGE,"E92.2"),sQuery(id+"F4.wireOp",EDGE,"E92.3"),sQuery(id+"F4.wireOp",EDGE,"E92.4"),sQuery(id+"F4.wireOp",EDGE,"E92.5"),sQuery(id+"F4.wireOp",EDGE,"E92.6"),sQuery(id+"F4.wireOp",EDGE,"E92.7"),sQuery(id+"F4.wireOp",EDGE,"E92.8"),sQuery(id+"F4.wireOp",EDGE,"E92.9"),sQuery(id+"F4.wireOp",EDGE,"E92.10"),sQuery(id+"F4.wireOp",EDGE,"E92.11"),sQuery(id+"F4.wireOp",EDGE,"E92.12"),sQuery(id+"F4.wireOp",EDGE,"E92.13"),sQuery(id+"F4.wireOp",EDGE,"E92.14"),sQuery(id+"F4.wireOp",EDGE,"E92.15"),sQuery(id+"F4.wireOp",EDGE,"E92.16"),sQuery(id+"F4.wireOp",EDGE,"E92.17"),sQuery(id+"F4.wireOp",EDGE,"E93"),sQuery(id+"F4.wireOp",EDGE,"E94")])],"isStart":false}),"instanceName":"1"})]});
            var Q32;
            Q32=makeQuery(id+"F6.boolean.opBoolean","INTERSECT",EDGE,{"derivedFrom":[makeQuery(id+"F1.opExtrude","SWEPT_FACE",FACE,{"disambiguationData":[OSD([sQuery(id+"F0.wireOp",EDGE,"E34"),sQuery(id+"F0.wireOp",EDGE,"E89")])]}),makeQuery(id+"F6.opPattern","COPY",FACE,{"derivedFrom":makeQuery(id+"F5.opExtrude","CAP_FACE",FACE,{"disambiguationData":[OSD([sQuery(id+"F4.wireOp",EDGE,"E92.0"),sQuery(id+"F4.wireOp",EDGE,"E92.1"),sQuery(id+"F4.wireOp",EDGE,"E92.2"),sQuery(id+"F4.wireOp",EDGE,"E92.3"),sQuery(id+"F4.wireOp",EDGE,"E92.4"),sQuery(id+"F4.wireOp",EDGE,"E92.5"),sQuery(id+"F4.wireOp",EDGE,"E92.6"),sQuery(id+"F4.wireOp",EDGE,"E92.7"),sQuery(id+"F4.wireOp",EDGE,"E92.8"),sQuery(id+"F4.wireOp",EDGE,"E92.9"),sQuery(id+"F4.wireOp",EDGE,"E92.10"),sQuery(id+"F4.wireOp",EDGE,"E92.11"),sQuery(id+"F4.wireOp",EDGE,"E92.12"),sQuery(id+"F4.wireOp",EDGE,"E92.13"),sQuery(id+"F4.wireOp",EDGE,"E92.14"),sQuery(id+"F4.wireOp",EDGE,"E92.15"),sQuery(id+"F4.wireOp",EDGE,"E92.16"),sQuery(id+"F4.wireOp",EDGE,"E92.17"),sQuery(id+"F4.wireOp",EDGE,"E93"),sQuery(id+"F4.wireOp",EDGE,"E94")])],"isStart":false}),"instanceName":"1"})]});
            var Q33;
            Q33=makeQuery(id+"F6.boolean.opBoolean","INTERSECT",EDGE,{"derivedFrom":[makeQuery(id+"F1.opExtrude","SWEPT_FACE",FACE,{"disambiguationData":[OSD([sQuery(id+"F0.wireOp",EDGE,"E29"),sQuery(id+"F0.wireOp",EDGE,"E75")])]}),makeQuery(id+"F6.opPattern","COPY",FACE,{"derivedFrom":makeQuery(id+"F5.opExtrude","CAP_FACE",FACE,{"disambiguationData":[OSD([sQuery(id+"F4.wireOp",EDGE,"E92.0"),sQuery(id+"F4.wireOp",EDGE,"E92.1"),sQuery(id+"F4.wireOp",EDGE,"E92.2"),sQuery(id+"F4.wireOp",EDGE,"E92.3"),sQuery(id+"F4.wireOp",EDGE,"E92.4"),sQuery(id+"F4.wireOp",EDGE,"E92.5"),sQuery(id+"F4.wireOp",EDGE,"E92.6"),sQuery(id+"F4.wireOp",EDGE,"E92.7"),sQuery(id+"F4.wireOp",EDGE,"E92.8"),sQuery(id+"F4.wireOp",EDGE,"E92.9"),sQuery(id+"F4.wireOp",EDGE,"E92.10"),sQuery(id+"F4.wireOp",EDGE,"E92.11"),sQuery(id+"F4.wireOp",EDGE,"E92.12"),sQuery(id+"F4.wireOp",EDGE,"E92.13"),sQuery(id+"F4.wireOp",EDGE,"E92.14"),sQuery(id+"F4.wireOp",EDGE,"E92.15"),sQuery(id+"F4.wireOp",EDGE,"E92.16"),sQuery(id+"F4.wireOp",EDGE,"E92.17"),sQuery(id+"F4.wireOp",EDGE,"E93"),sQuery(id+"F4.wireOp",EDGE,"E94")])],"isStart":false}),"instanceName":"1"})]});
            var Q34;
            Q34=makeQuery(id+"F6.boolean.opBoolean","INTERSECT",EDGE,{"derivedFrom":[makeQuery(id+"F1.opExtrude","SWEPT_FACE",FACE,{"disambiguationData":[OSD([sQuery(id+"F0.wireOp",EDGE,"E25"),sQuery(id+"F0.wireOp",EDGE,"E73")])]}),makeQuery(id+"F6.opPattern","COPY",FACE,{"derivedFrom":makeQuery(id+"F5.opExtrude","CAP_FACE",FACE,{"disambiguationData":[OSD([sQuery(id+"F4.wireOp",EDGE,"E92.0"),sQuery(id+"F4.wireOp",EDGE,"E92.1"),sQuery(id+"F4.wireOp",EDGE,"E92.2"),sQuery(id+"F4.wireOp",EDGE,"E92.3"),sQuery(id+"F4.wireOp",EDGE,"E92.4"),sQuery(id+"F4.wireOp",EDGE,"E92.5"),sQuery(id+"F4.wireOp",EDGE,"E92.6"),sQuery(id+"F4.wireOp",EDGE,"E92.7"),sQuery(id+"F4.wireOp",EDGE,"E92.8"),sQuery(id+"F4.wireOp",EDGE,"E92.9"),sQuery(id+"F4.wireOp",EDGE,"E92.10"),sQuery(id+"F4.wireOp",EDGE,"E92.11"),sQuery(id+"F4.wireOp",EDGE,"E92.12"),sQuery(id+"F4.wireOp",EDGE,"E92.13"),sQuery(id+"F4.wireOp",EDGE,"E92.14"),sQuery(id+"F4.wireOp",EDGE,"E92.15"),sQuery(id+"F4.wireOp",EDGE,"E92.16"),sQuery(id+"F4.wireOp",EDGE,"E92.17"),sQuery(id+"F4.wireOp",EDGE,"E93"),sQuery(id+"F4.wireOp",EDGE,"E94")])],"isStart":false}),"instanceName":"1"})]});
            var Q35;
            Q35=makeQuery(id+"F6.boolean.opBoolean","INTERSECT",EDGE,{"derivedFrom":[makeQuery(id+"F1.opExtrude","SWEPT_FACE",FACE,{"disambiguationData":[OSD([sQuery(id+"F0.wireOp",EDGE,"E20"),sQuery(id+"F0.wireOp",EDGE,"E81")])]}),makeQuery(id+"F6.opPattern","COPY",FACE,{"derivedFrom":makeQuery(id+"F5.opExtrude","CAP_FACE",FACE,{"disambiguationData":[OSD([sQuery(id+"F4.wireOp",EDGE,"E92.0"),sQuery(id+"F4.wireOp",EDGE,"E92.1"),sQuery(id+"F4.wireOp",EDGE,"E92.2"),sQuery(id+"F4.wireOp",EDGE,"E92.3"),sQuery(id+"F4.wireOp",EDGE,"E92.4"),sQuery(id+"F4.wireOp",EDGE,"E92.5"),sQuery(id+"F4.wireOp",EDGE,"E92.6"),sQuery(id+"F4.wireOp",EDGE,"E92.7"),sQuery(id+"F4.wireOp",EDGE,"E92.8"),sQuery(id+"F4.wireOp",EDGE,"E92.9"),sQuery(id+"F4.wireOp",EDGE,"E92.10"),sQuery(id+"F4.wireOp",EDGE,"E92.11"),sQuery(id+"F4.wireOp",EDGE,"E92.12"),sQuery(id+"F4.wireOp",EDGE,"E92.13"),sQuery(id+"F4.wireOp",EDGE,"E92.14"),sQuery(id+"F4.wireOp",EDGE,"E92.15"),sQuery(id+"F4.wireOp",EDGE,"E92.16"),sQuery(id+"F4.wireOp",EDGE,"E92.17"),sQuery(id+"F4.wireOp",EDGE,"E93"),sQuery(id+"F4.wireOp",EDGE,"E94")])],"isStart":false}),"instanceName":"1"})]});
            var Q36;
            Q36=makeQuery(id+"F6.boolean.opBoolean","INTERSECT",EDGE,{"derivedFrom":[makeQuery(id+"F1.opExtrude","SWEPT_FACE",FACE,{"disambiguationData":[OSD([sQuery(id+"F0.wireOp",EDGE,"E17"),sQuery(id+"F0.wireOp",EDGE,"E80")])]}),makeQuery(id+"F6.opPattern","COPY",FACE,{"derivedFrom":makeQuery(id+"F5.opExtrude","CAP_FACE",FACE,{"disambiguationData":[OSD([sQuery(id+"F4.wireOp",EDGE,"E92.0"),sQuery(id+"F4.wireOp",EDGE,"E92.1"),sQuery(id+"F4.wireOp",EDGE,"E92.2"),sQuery(id+"F4.wireOp",EDGE,"E92.3"),sQuery(id+"F4.wireOp",EDGE,"E92.4"),sQuery(id+"F4.wireOp",EDGE,"E92.5"),sQuery(id+"F4.wireOp",EDGE,"E92.6"),sQuery(id+"F4.wireOp",EDGE,"E92.7"),sQuery(id+"F4.wireOp",EDGE,"E92.8"),sQuery(id+"F4.wireOp",EDGE,"E92.9"),sQuery(id+"F4.wireOp",EDGE,"E92.10"),sQuery(id+"F4.wireOp",EDGE,"E92.11"),sQuery(id+"F4.wireOp",EDGE,"E92.12"),sQuery(id+"F4.wireOp",EDGE,"E92.13"),sQuery(id+"F4.wireOp",EDGE,"E92.14"),sQuery(id+"F4.wireOp",EDGE,"E92.15"),sQuery(id+"F4.wireOp",EDGE,"E92.16"),sQuery(id+"F4.wireOp",EDGE,"E92.17"),sQuery(id+"F4.wireOp",EDGE,"E93"),sQuery(id+"F4.wireOp",EDGE,"E94")])],"isStart":false}),"instanceName":"1"})]});
            var Q37;
            Q37=makeQuery(id+"F6.boolean.opBoolean","INTERSECT",EDGE,{"derivedFrom":[makeQuery(id+"F1.opExtrude","SWEPT_FACE",FACE,{"disambiguationData":[OSD([sQuery(id+"F0.wireOp",EDGE,"E13"),sQuery(id+"F0.wireOp",EDGE,"E63")])]}),makeQuery(id+"F6.opPattern","COPY",FACE,{"derivedFrom":makeQuery(id+"F5.opExtrude","CAP_FACE",FACE,{"disambiguationData":[OSD([sQuery(id+"F4.wireOp",EDGE,"E92.0"),sQuery(id+"F4.wireOp",EDGE,"E92.1"),sQuery(id+"F4.wireOp",EDGE,"E92.2"),sQuery(id+"F4.wireOp",EDGE,"E92.3"),sQuery(id+"F4.wireOp",EDGE,"E92.4"),sQuery(id+"F4.wireOp",EDGE,"E92.5"),sQuery(id+"F4.wireOp",EDGE,"E92.6"),sQuery(id+"F4.wireOp",EDGE,"E92.7"),sQuery(id+"F4.wireOp",EDGE,"E92.8"),sQuery(id+"F4.wireOp",EDGE,"E92.9"),sQuery(id+"F4.wireOp",EDGE,"E92.10"),sQuery(id+"F4.wireOp",EDGE,"E92.11"),sQuery(id+"F4.wireOp",EDGE,"E92.12"),sQuery(id+"F4.wireOp",EDGE,"E92.13"),sQuery(id+"F4.wireOp",EDGE,"E92.14"),sQuery(id+"F4.wireOp",EDGE,"E92.15"),sQuery(id+"F4.wireOp",EDGE,"E92.16"),sQuery(id+"F4.wireOp",EDGE,"E92.17"),sQuery(id+"F4.wireOp",EDGE,"E93"),sQuery(id+"F4.wireOp",EDGE,"E94")])],"isStart":false}),"instanceName":"1"})]});
            var Q38;
            Q38=makeQuery(id+"F6.boolean.opBoolean","INTERSECT",EDGE,{"derivedFrom":[makeQuery(id+"F1.opExtrude","SWEPT_FACE",FACE,{"disambiguationData":[OSD([sQuery(id+"F0.wireOp",EDGE,"E9"),sQuery(id+"F0.wireOp",EDGE,"E60")])]}),makeQuery(id+"F6.opPattern","COPY",FACE,{"derivedFrom":makeQuery(id+"F5.opExtrude","CAP_FACE",FACE,{"disambiguationData":[OSD([sQuery(id+"F4.wireOp",EDGE,"E92.0"),sQuery(id+"F4.wireOp",EDGE,"E92.1"),sQuery(id+"F4.wireOp",EDGE,"E92.2"),sQuery(id+"F4.wireOp",EDGE,"E92.3"),sQuery(id+"F4.wireOp",EDGE,"E92.4"),sQuery(id+"F4.wireOp",EDGE,"E92.5"),sQuery(id+"F4.wireOp",EDGE,"E92.6"),sQuery(id+"F4.wireOp",EDGE,"E92.7"),sQuery(id+"F4.wireOp",EDGE,"E92.8"),sQuery(id+"F4.wireOp",EDGE,"E92.9"),sQuery(id+"F4.wireOp",EDGE,"E92.10"),sQuery(id+"F4.wireOp",EDGE,"E92.11"),sQuery(id+"F4.wireOp",EDGE,"E92.12"),sQuery(id+"F4.wireOp",EDGE,"E92.13"),sQuery(id+"F4.wireOp",EDGE,"E92.14"),sQuery(id+"F4.wireOp",EDGE,"E92.15"),sQuery(id+"F4.wireOp",EDGE,"E92.16"),sQuery(id+"F4.wireOp",EDGE,"E92.17"),sQuery(id+"F4.wireOp",EDGE,"E93"),sQuery(id+"F4.wireOp",EDGE,"E94")])],"isStart":false}),"instanceName":"1"})]});
            var Q39;
            Q39=makeQuery(id+"F6.boolean.opBoolean","INTERSECT",EDGE,{"derivedFrom":[makeQuery(id+"F1.opExtrude","SWEPT_FACE",FACE,{"disambiguationData":[OSD([sQuery(id+"F0.wireOp",EDGE,"E40"),sQuery(id+"F0.wireOp",EDGE,"E69")])]}),makeQuery(id+"F5.opExtrude","CAP_FACE",FACE,{"disambiguationData":[OSD([sQuery(id+"F4.wireOp",EDGE,"E92.0"),sQuery(id+"F4.wireOp",EDGE,"E92.1"),sQuery(id+"F4.wireOp",EDGE,"E92.2"),sQuery(id+"F4.wireOp",EDGE,"E92.3"),sQuery(id+"F4.wireOp",EDGE,"E92.4"),sQuery(id+"F4.wireOp",EDGE,"E92.5"),sQuery(id+"F4.wireOp",EDGE,"E92.6"),sQuery(id+"F4.wireOp",EDGE,"E92.7"),sQuery(id+"F4.wireOp",EDGE,"E92.8"),sQuery(id+"F4.wireOp",EDGE,"E92.9"),sQuery(id+"F4.wireOp",EDGE,"E92.10"),sQuery(id+"F4.wireOp",EDGE,"E92.11"),sQuery(id+"F4.wireOp",EDGE,"E92.12"),sQuery(id+"F4.wireOp",EDGE,"E92.13"),sQuery(id+"F4.wireOp",EDGE,"E92.14"),sQuery(id+"F4.wireOp",EDGE,"E92.15"),sQuery(id+"F4.wireOp",EDGE,"E92.16"),sQuery(id+"F4.wireOp",EDGE,"E92.17"),sQuery(id+"F4.wireOp",EDGE,"E93"),sQuery(id+"F4.wireOp",EDGE,"E94")])],"isStart":false})]});
            fillet(context, id + "F12", {"entities" : qUnion([Q0, Q1, Q2, Q3, Q4, Q5, Q6, Q7, Q8, Q9, Q10, Q11, Q12, Q13, Q14, Q15, Q16, Q17, Q18, Q19, Q20, Q21, Q22, Q23, Q24, Q25, Q26, Q27, Q28, Q29, Q30, Q31, Q32, Q33, Q34, Q35, Q36, Q37, Q38, Q39]), "radius" : 12.7 * mm, "tangentPropagation" : true, "allowEdgeOverflow" : false});
        }
        {
            var Q0;
            Q0=makeQuery(id+"F6.boolean.opBoolean","INTERSECT",EDGE,{"derivedFrom":[makeQuery(id+"F1.opExtrude","SWEPT_FACE",FACE,{"disambiguationData":[OSD([sQuery(id+"F0.wireOp",EDGE,"E61")])]}),makeQuery(id+"F6.opPattern","COPY",FACE,{"derivedFrom":makeQuery(id+"F5.opExtrude","CAP_FACE",FACE,{"disambiguationData":[OSD([sQuery(id+"F4.wireOp",EDGE,"E92.0"),sQuery(id+"F4.wireOp",EDGE,"E92.1"),sQuery(id+"F4.wireOp",EDGE,"E92.2"),sQuery(id+"F4.wireOp",EDGE,"E92.3"),sQuery(id+"F4.wireOp",EDGE,"E92.4"),sQuery(id+"F4.wireOp",EDGE,"E92.5"),sQuery(id+"F4.wireOp",EDGE,"E92.6"),sQuery(id+"F4.wireOp",EDGE,"E92.7"),sQuery(id+"F4.wireOp",EDGE,"E92.8"),sQuery(id+"F4.wireOp",EDGE,"E92.9"),sQuery(id+"F4.wireOp",EDGE,"E92.10"),sQuery(id+"F4.wireOp",EDGE,"E92.11"),sQuery(id+"F4.wireOp",EDGE,"E92.12"),sQuery(id+"F4.wireOp",EDGE,"E92.13"),sQuery(id+"F4.wireOp",EDGE,"E92.14"),sQuery(id+"F4.wireOp",EDGE,"E92.15"),sQuery(id+"F4.wireOp",EDGE,"E92.16"),sQuery(id+"F4.wireOp",EDGE,"E92.17"),sQuery(id+"F4.wireOp",EDGE,"E93"),sQuery(id+"F4.wireOp",EDGE,"E94")])],"isStart":false}),"instanceName":"1"})]});
            var Q1;
            Q1=makeQuery(id+"F6.boolean.opBoolean","INTERSECT",EDGE,{"derivedFrom":[makeQuery(id+"F1.opExtrude","SWEPT_FACE",FACE,{"disambiguationData":[OSD([sQuery(id+"F0.wireOp",EDGE,"E64")])]}),makeQuery(id+"F6.opPattern","COPY",FACE,{"derivedFrom":makeQuery(id+"F5.opExtrude","CAP_FACE",FACE,{"disambiguationData":[OSD([sQuery(id+"F4.wireOp",EDGE,"E92.0"),sQuery(id+"F4.wireOp",EDGE,"E92.1"),sQuery(id+"F4.wireOp",EDGE,"E92.2"),sQuery(id+"F4.wireOp",EDGE,"E92.3"),sQuery(id+"F4.wireOp",EDGE,"E92.4"),sQuery(id+"F4.wireOp",EDGE,"E92.5"),sQuery(id+"F4.wireOp",EDGE,"E92.6"),sQuery(id+"F4.wireOp",EDGE,"E92.7"),sQuery(id+"F4.wireOp",EDGE,"E92.8"),sQuery(id+"F4.wireOp",EDGE,"E92.9"),sQuery(id+"F4.wireOp",EDGE,"E92.10"),sQuery(id+"F4.wireOp",EDGE,"E92.11"),sQuery(id+"F4.wireOp",EDGE,"E92.12"),sQuery(id+"F4.wireOp",EDGE,"E92.13"),sQuery(id+"F4.wireOp",EDGE,"E92.14"),sQuery(id+"F4.wireOp",EDGE,"E92.15"),sQuery(id+"F4.wireOp",EDGE,"E92.16"),sQuery(id+"F4.wireOp",EDGE,"E92.17"),sQuery(id+"F4.wireOp",EDGE,"E93"),sQuery(id+"F4.wireOp",EDGE,"E94")])],"isStart":false}),"instanceName":"1"})]});
            var Q2;
            Q2=makeQuery(id+"F6.boolean.opBoolean","INTERSECT",EDGE,{"derivedFrom":[makeQuery(id+"F1.opExtrude","SWEPT_FACE",FACE,{"disambiguationData":[OSD([sQuery(id+"F0.wireOp",EDGE,"E79")])]}),makeQuery(id+"F6.opPattern","COPY",FACE,{"derivedFrom":makeQuery(id+"F5.opExtrude","CAP_FACE",FACE,{"disambiguationData":[OSD([sQuery(id+"F4.wireOp",EDGE,"E92.0"),sQuery(id+"F4.wireOp",EDGE,"E92.1"),sQuery(id+"F4.wireOp",EDGE,"E92.2"),sQuery(id+"F4.wireOp",EDGE,"E92.3"),sQuery(id+"F4.wireOp",EDGE,"E92.4"),sQuery(id+"F4.wireOp",EDGE,"E92.5"),sQuery(id+"F4.wireOp",EDGE,"E92.6"),sQuery(id+"F4.wireOp",EDGE,"E92.7"),sQuery(id+"F4.wireOp",EDGE,"E92.8"),sQuery(id+"F4.wireOp",EDGE,"E92.9"),sQuery(id+"F4.wireOp",EDGE,"E92.10"),sQuery(id+"F4.wireOp",EDGE,"E92.11"),sQuery(id+"F4.wireOp",EDGE,"E92.12"),sQuery(id+"F4.wireOp",EDGE,"E92.13"),sQuery(id+"F4.wireOp",EDGE,"E92.14"),sQuery(id+"F4.wireOp",EDGE,"E92.15"),sQuery(id+"F4.wireOp",EDGE,"E92.16"),sQuery(id+"F4.wireOp",EDGE,"E92.17"),sQuery(id+"F4.wireOp",EDGE,"E93"),sQuery(id+"F4.wireOp",EDGE,"E94")])],"isStart":false}),"instanceName":"1"})]});
            var Q3;
            Q3=makeQuery(id+"F6.boolean.opBoolean","INTERSECT",EDGE,{"derivedFrom":[makeQuery(id+"F1.opExtrude","SWEPT_FACE",FACE,{"disambiguationData":[OSD([sQuery(id+"F0.wireOp",EDGE,"E66")])]}),makeQuery(id+"F6.opPattern","COPY",FACE,{"derivedFrom":makeQuery(id+"F5.opExtrude","CAP_FACE",FACE,{"disambiguationData":[OSD([sQuery(id+"F4.wireOp",EDGE,"E92.0"),sQuery(id+"F4.wireOp",EDGE,"E92.1"),sQuery(id+"F4.wireOp",EDGE,"E92.2"),sQuery(id+"F4.wireOp",EDGE,"E92.3"),sQuery(id+"F4.wireOp",EDGE,"E92.4"),sQuery(id+"F4.wireOp",EDGE,"E92.5"),sQuery(id+"F4.wireOp",EDGE,"E92.6"),sQuery(id+"F4.wireOp",EDGE,"E92.7"),sQuery(id+"F4.wireOp",EDGE,"E92.8"),sQuery(id+"F4.wireOp",EDGE,"E92.9"),sQuery(id+"F4.wireOp",EDGE,"E92.10"),sQuery(id+"F4.wireOp",EDGE,"E92.11"),sQuery(id+"F4.wireOp",EDGE,"E92.12"),sQuery(id+"F4.wireOp",EDGE,"E92.13"),sQuery(id+"F4.wireOp",EDGE,"E92.14"),sQuery(id+"F4.wireOp",EDGE,"E92.15"),sQuery(id+"F4.wireOp",EDGE,"E92.16"),sQuery(id+"F4.wireOp",EDGE,"E92.17"),sQuery(id+"F4.wireOp",EDGE,"E93"),sQuery(id+"F4.wireOp",EDGE,"E94")])],"isStart":false}),"instanceName":"1"})]});
            var Q4;
            Q4=makeQuery(id+"F6.boolean.opBoolean","INTERSECT",EDGE,{"derivedFrom":[makeQuery(id+"F1.opExtrude","SWEPT_FACE",FACE,{"disambiguationData":[OSD([sQuery(id+"F0.wireOp",EDGE,"E84")])]}),makeQuery(id+"F6.opPattern","COPY",FACE,{"derivedFrom":makeQuery(id+"F5.opExtrude","CAP_FACE",FACE,{"disambiguationData":[OSD([sQuery(id+"F4.wireOp",EDGE,"E92.0"),sQuery(id+"F4.wireOp",EDGE,"E92.1"),sQuery(id+"F4.wireOp",EDGE,"E92.2"),sQuery(id+"F4.wireOp",EDGE,"E92.3"),sQuery(id+"F4.wireOp",EDGE,"E92.4"),sQuery(id+"F4.wireOp",EDGE,"E92.5"),sQuery(id+"F4.wireOp",EDGE,"E92.6"),sQuery(id+"F4.wireOp",EDGE,"E92.7"),sQuery(id+"F4.wireOp",EDGE,"E92.8"),sQuery(id+"F4.wireOp",EDGE,"E92.9"),sQuery(id+"F4.wireOp",EDGE,"E92.10"),sQuery(id+"F4.wireOp",EDGE,"E92.11"),sQuery(id+"F4.wireOp",EDGE,"E92.12"),sQuery(id+"F4.wireOp",EDGE,"E92.13"),sQuery(id+"F4.wireOp",EDGE,"E92.14"),sQuery(id+"F4.wireOp",EDGE,"E92.15"),sQuery(id+"F4.wireOp",EDGE,"E92.16"),sQuery(id+"F4.wireOp",EDGE,"E92.17"),sQuery(id+"F4.wireOp",EDGE,"E93"),sQuery(id+"F4.wireOp",EDGE,"E94")])],"isStart":false}),"instanceName":"1"})]});
            var Q5;
            Q5=makeQuery(id+"F6.boolean.opBoolean","INTERSECT",EDGE,{"derivedFrom":[makeQuery(id+"F1.opExtrude","SWEPT_FACE",FACE,{"disambiguationData":[OSD([sQuery(id+"F0.wireOp",EDGE,"E86")])]}),makeQuery(id+"F6.opPattern","COPY",FACE,{"derivedFrom":makeQuery(id+"F5.opExtrude","CAP_FACE",FACE,{"disambiguationData":[OSD([sQuery(id+"F4.wireOp",EDGE,"E92.0"),sQuery(id+"F4.wireOp",EDGE,"E92.1"),sQuery(id+"F4.wireOp",EDGE,"E92.2"),sQuery(id+"F4.wireOp",EDGE,"E92.3"),sQuery(id+"F4.wireOp",EDGE,"E92.4"),sQuery(id+"F4.wireOp",EDGE,"E92.5"),sQuery(id+"F4.wireOp",EDGE,"E92.6"),sQuery(id+"F4.wireOp",EDGE,"E92.7"),sQuery(id+"F4.wireOp",EDGE,"E92.8"),sQuery(id+"F4.wireOp",EDGE,"E92.9"),sQuery(id+"F4.wireOp",EDGE,"E92.10"),sQuery(id+"F4.wireOp",EDGE,"E92.11"),sQuery(id+"F4.wireOp",EDGE,"E92.12"),sQuery(id+"F4.wireOp",EDGE,"E92.13"),sQuery(id+"F4.wireOp",EDGE,"E92.14"),sQuery(id+"F4.wireOp",EDGE,"E92.15"),sQuery(id+"F4.wireOp",EDGE,"E92.16"),sQuery(id+"F4.wireOp",EDGE,"E92.17"),sQuery(id+"F4.wireOp",EDGE,"E93"),sQuery(id+"F4.wireOp",EDGE,"E94")])],"isStart":false}),"instanceName":"1"})]});
            var Q6;
            Q6=makeQuery(id+"F6.boolean.opBoolean","INTERSECT",EDGE,{"derivedFrom":[makeQuery(id+"F1.opExtrude","SWEPT_FACE",FACE,{"disambiguationData":[OSD([sQuery(id+"F0.wireOp",EDGE,"E88")])]}),makeQuery(id+"F6.opPattern","COPY",FACE,{"derivedFrom":makeQuery(id+"F5.opExtrude","CAP_FACE",FACE,{"disambiguationData":[OSD([sQuery(id+"F4.wireOp",EDGE,"E92.0"),sQuery(id+"F4.wireOp",EDGE,"E92.1"),sQuery(id+"F4.wireOp",EDGE,"E92.2"),sQuery(id+"F4.wireOp",EDGE,"E92.3"),sQuery(id+"F4.wireOp",EDGE,"E92.4"),sQuery(id+"F4.wireOp",EDGE,"E92.5"),sQuery(id+"F4.wireOp",EDGE,"E92.6"),sQuery(id+"F4.wireOp",EDGE,"E92.7"),sQuery(id+"F4.wireOp",EDGE,"E92.8"),sQuery(id+"F4.wireOp",EDGE,"E92.9"),sQuery(id+"F4.wireOp",EDGE,"E92.10"),sQuery(id+"F4.wireOp",EDGE,"E92.11"),sQuery(id+"F4.wireOp",EDGE,"E92.12"),sQuery(id+"F4.wireOp",EDGE,"E92.13"),sQuery(id+"F4.wireOp",EDGE,"E92.14"),sQuery(id+"F4.wireOp",EDGE,"E92.15"),sQuery(id+"F4.wireOp",EDGE,"E92.16"),sQuery(id+"F4.wireOp",EDGE,"E92.17"),sQuery(id+"F4.wireOp",EDGE,"E93"),sQuery(id+"F4.wireOp",EDGE,"E94")])],"isStart":false}),"instanceName":"1"})]});
            var Q7;
            Q7=makeQuery(id+"F6.boolean.opBoolean","INTERSECT",EDGE,{"derivedFrom":[makeQuery(id+"F1.opExtrude","SWEPT_FACE",FACE,{"disambiguationData":[OSD([sQuery(id+"F0.wireOp",EDGE,"E68")])]}),makeQuery(id+"F6.opPattern","COPY",FACE,{"derivedFrom":makeQuery(id+"F5.opExtrude","CAP_FACE",FACE,{"disambiguationData":[OSD([sQuery(id+"F4.wireOp",EDGE,"E92.0"),sQuery(id+"F4.wireOp",EDGE,"E92.1"),sQuery(id+"F4.wireOp",EDGE,"E92.2"),sQuery(id+"F4.wireOp",EDGE,"E92.3"),sQuery(id+"F4.wireOp",EDGE,"E92.4"),sQuery(id+"F4.wireOp",EDGE,"E92.5"),sQuery(id+"F4.wireOp",EDGE,"E92.6"),sQuery(id+"F4.wireOp",EDGE,"E92.7"),sQuery(id+"F4.wireOp",EDGE,"E92.8"),sQuery(id+"F4.wireOp",EDGE,"E92.9"),sQuery(id+"F4.wireOp",EDGE,"E92.10"),sQuery(id+"F4.wireOp",EDGE,"E92.11"),sQuery(id+"F4.wireOp",EDGE,"E92.12"),sQuery(id+"F4.wireOp",EDGE,"E92.13"),sQuery(id+"F4.wireOp",EDGE,"E92.14"),sQuery(id+"F4.wireOp",EDGE,"E92.15"),sQuery(id+"F4.wireOp",EDGE,"E92.16"),sQuery(id+"F4.wireOp",EDGE,"E92.17"),sQuery(id+"F4.wireOp",EDGE,"E93"),sQuery(id+"F4.wireOp",EDGE,"E94")])],"isStart":false}),"instanceName":"1"})]});
            var Q8;
            Q8=makeQuery(id+"F6.boolean.opBoolean","INTERSECT",EDGE,{"derivedFrom":[makeQuery(id+"F1.opExtrude","SWEPT_FACE",FACE,{"disambiguationData":[OSD([sQuery(id+"F0.wireOp",EDGE,"E91")])]}),makeQuery(id+"F6.opPattern","COPY",FACE,{"derivedFrom":makeQuery(id+"F5.opExtrude","CAP_FACE",FACE,{"disambiguationData":[OSD([sQuery(id+"F4.wireOp",EDGE,"E92.0"),sQuery(id+"F4.wireOp",EDGE,"E92.1"),sQuery(id+"F4.wireOp",EDGE,"E92.2"),sQuery(id+"F4.wireOp",EDGE,"E92.3"),sQuery(id+"F4.wireOp",EDGE,"E92.4"),sQuery(id+"F4.wireOp",EDGE,"E92.5"),sQuery(id+"F4.wireOp",EDGE,"E92.6"),sQuery(id+"F4.wireOp",EDGE,"E92.7"),sQuery(id+"F4.wireOp",EDGE,"E92.8"),sQuery(id+"F4.wireOp",EDGE,"E92.9"),sQuery(id+"F4.wireOp",EDGE,"E92.10"),sQuery(id+"F4.wireOp",EDGE,"E92.11"),sQuery(id+"F4.wireOp",EDGE,"E92.12"),sQuery(id+"F4.wireOp",EDGE,"E92.13"),sQuery(id+"F4.wireOp",EDGE,"E92.14"),sQuery(id+"F4.wireOp",EDGE,"E92.15"),sQuery(id+"F4.wireOp",EDGE,"E92.16"),sQuery(id+"F4.wireOp",EDGE,"E92.17"),sQuery(id+"F4.wireOp",EDGE,"E93"),sQuery(id+"F4.wireOp",EDGE,"E94")])],"isStart":false}),"instanceName":"1"})]});
            var Q9;
            Q9=makeQuery(id+"F6.boolean.opBoolean","INTERSECT",EDGE,{"derivedFrom":[makeQuery(id+"F1.opExtrude","SWEPT_FACE",FACE,{"disambiguationData":[OSD([sQuery(id+"F0.wireOp",EDGE,"E71")])]}),makeQuery(id+"F6.opPattern","COPY",FACE,{"derivedFrom":makeQuery(id+"F5.opExtrude","CAP_FACE",FACE,{"disambiguationData":[OSD([sQuery(id+"F4.wireOp",EDGE,"E92.0"),sQuery(id+"F4.wireOp",EDGE,"E92.1"),sQuery(id+"F4.wireOp",EDGE,"E92.2"),sQuery(id+"F4.wireOp",EDGE,"E92.3"),sQuery(id+"F4.wireOp",EDGE,"E92.4"),sQuery(id+"F4.wireOp",EDGE,"E92.5"),sQuery(id+"F4.wireOp",EDGE,"E92.6"),sQuery(id+"F4.wireOp",EDGE,"E92.7"),sQuery(id+"F4.wireOp",EDGE,"E92.8"),sQuery(id+"F4.wireOp",EDGE,"E92.9"),sQuery(id+"F4.wireOp",EDGE,"E92.10"),sQuery(id+"F4.wireOp",EDGE,"E92.11"),sQuery(id+"F4.wireOp",EDGE,"E92.12"),sQuery(id+"F4.wireOp",EDGE,"E92.13"),sQuery(id+"F4.wireOp",EDGE,"E92.14"),sQuery(id+"F4.wireOp",EDGE,"E92.15"),sQuery(id+"F4.wireOp",EDGE,"E92.16"),sQuery(id+"F4.wireOp",EDGE,"E92.17"),sQuery(id+"F4.wireOp",EDGE,"E93"),sQuery(id+"F4.wireOp",EDGE,"E94")])],"isStart":false}),"instanceName":"1"})]});
            var Q10;
            Q10=makeQuery(id+"F6.boolean.opBoolean","INTERSECT",EDGE,{"derivedFrom":[makeQuery(id+"F1.opExtrude","SWEPT_FACE",FACE,{"disambiguationData":[OSD([sQuery(id+"F0.wireOp",EDGE,"E71")])]}),makeQuery(id+"F5.opExtrude","CAP_FACE",FACE,{"disambiguationData":[OSD([sQuery(id+"F4.wireOp",EDGE,"E92.0"),sQuery(id+"F4.wireOp",EDGE,"E92.1"),sQuery(id+"F4.wireOp",EDGE,"E92.2"),sQuery(id+"F4.wireOp",EDGE,"E92.3"),sQuery(id+"F4.wireOp",EDGE,"E92.4"),sQuery(id+"F4.wireOp",EDGE,"E92.5"),sQuery(id+"F4.wireOp",EDGE,"E92.6"),sQuery(id+"F4.wireOp",EDGE,"E92.7"),sQuery(id+"F4.wireOp",EDGE,"E92.8"),sQuery(id+"F4.wireOp",EDGE,"E92.9"),sQuery(id+"F4.wireOp",EDGE,"E92.10"),sQuery(id+"F4.wireOp",EDGE,"E92.11"),sQuery(id+"F4.wireOp",EDGE,"E92.12"),sQuery(id+"F4.wireOp",EDGE,"E92.13"),sQuery(id+"F4.wireOp",EDGE,"E92.14"),sQuery(id+"F4.wireOp",EDGE,"E92.15"),sQuery(id+"F4.wireOp",EDGE,"E92.16"),sQuery(id+"F4.wireOp",EDGE,"E92.17"),sQuery(id+"F4.wireOp",EDGE,"E93"),sQuery(id+"F4.wireOp",EDGE,"E94")])],"isStart":false})]});
            var Q11;
            Q11=makeQuery(id+"F6.boolean.opBoolean","INTERSECT",EDGE,{"derivedFrom":[makeQuery(id+"F1.opExtrude","SWEPT_FACE",FACE,{"disambiguationData":[OSD([sQuery(id+"F0.wireOp",EDGE,"E91")])]}),makeQuery(id+"F5.opExtrude","CAP_FACE",FACE,{"disambiguationData":[OSD([sQuery(id+"F4.wireOp",EDGE,"E92.0"),sQuery(id+"F4.wireOp",EDGE,"E92.1"),sQuery(id+"F4.wireOp",EDGE,"E92.2"),sQuery(id+"F4.wireOp",EDGE,"E92.3"),sQuery(id+"F4.wireOp",EDGE,"E92.4"),sQuery(id+"F4.wireOp",EDGE,"E92.5"),sQuery(id+"F4.wireOp",EDGE,"E92.6"),sQuery(id+"F4.wireOp",EDGE,"E92.7"),sQuery(id+"F4.wireOp",EDGE,"E92.8"),sQuery(id+"F4.wireOp",EDGE,"E92.9"),sQuery(id+"F4.wireOp",EDGE,"E92.10"),sQuery(id+"F4.wireOp",EDGE,"E92.11"),sQuery(id+"F4.wireOp",EDGE,"E92.12"),sQuery(id+"F4.wireOp",EDGE,"E92.13"),sQuery(id+"F4.wireOp",EDGE,"E92.14"),sQuery(id+"F4.wireOp",EDGE,"E92.15"),sQuery(id+"F4.wireOp",EDGE,"E92.16"),sQuery(id+"F4.wireOp",EDGE,"E92.17"),sQuery(id+"F4.wireOp",EDGE,"E93"),sQuery(id+"F4.wireOp",EDGE,"E94")])],"isStart":false})]});
            var Q12;
            Q12=makeQuery(id+"F6.boolean.opBoolean","INTERSECT",EDGE,{"derivedFrom":[makeQuery(id+"F1.opExtrude","SWEPT_FACE",FACE,{"disambiguationData":[OSD([sQuery(id+"F0.wireOp",EDGE,"E68")])]}),makeQuery(id+"F5.opExtrude","CAP_FACE",FACE,{"disambiguationData":[OSD([sQuery(id+"F4.wireOp",EDGE,"E92.0"),sQuery(id+"F4.wireOp",EDGE,"E92.1"),sQuery(id+"F4.wireOp",EDGE,"E92.2"),sQuery(id+"F4.wireOp",EDGE,"E92.3"),sQuery(id+"F4.wireOp",EDGE,"E92.4"),sQuery(id+"F4.wireOp",EDGE,"E92.5"),sQuery(id+"F4.wireOp",EDGE,"E92.6"),sQuery(id+"F4.wireOp",EDGE,"E92.7"),sQuery(id+"F4.wireOp",EDGE,"E92.8"),sQuery(id+"F4.wireOp",EDGE,"E92.9"),sQuery(id+"F4.wireOp",EDGE,"E92.10"),sQuery(id+"F4.wireOp",EDGE,"E92.11"),sQuery(id+"F4.wireOp",EDGE,"E92.12"),sQuery(id+"F4.wireOp",EDGE,"E92.13"),sQuery(id+"F4.wireOp",EDGE,"E92.14"),sQuery(id+"F4.wireOp",EDGE,"E92.15"),sQuery(id+"F4.wireOp",EDGE,"E92.16"),sQuery(id+"F4.wireOp",EDGE,"E92.17"),sQuery(id+"F4.wireOp",EDGE,"E93"),sQuery(id+"F4.wireOp",EDGE,"E94")])],"isStart":false})]});
            var Q13;
            Q13=makeQuery(id+"F6.boolean.opBoolean","INTERSECT",EDGE,{"derivedFrom":[makeQuery(id+"F1.opExtrude","SWEPT_FACE",FACE,{"disambiguationData":[OSD([sQuery(id+"F0.wireOp",EDGE,"E88")])]}),makeQuery(id+"F5.opExtrude","CAP_FACE",FACE,{"disambiguationData":[OSD([sQuery(id+"F4.wireOp",EDGE,"E92.0"),sQuery(id+"F4.wireOp",EDGE,"E92.1"),sQuery(id+"F4.wireOp",EDGE,"E92.2"),sQuery(id+"F4.wireOp",EDGE,"E92.3"),sQuery(id+"F4.wireOp",EDGE,"E92.4"),sQuery(id+"F4.wireOp",EDGE,"E92.5"),sQuery(id+"F4.wireOp",EDGE,"E92.6"),sQuery(id+"F4.wireOp",EDGE,"E92.7"),sQuery(id+"F4.wireOp",EDGE,"E92.8"),sQuery(id+"F4.wireOp",EDGE,"E92.9"),sQuery(id+"F4.wireOp",EDGE,"E92.10"),sQuery(id+"F4.wireOp",EDGE,"E92.11"),sQuery(id+"F4.wireOp",EDGE,"E92.12"),sQuery(id+"F4.wireOp",EDGE,"E92.13"),sQuery(id+"F4.wireOp",EDGE,"E92.14"),sQuery(id+"F4.wireOp",EDGE,"E92.15"),sQuery(id+"F4.wireOp",EDGE,"E92.16"),sQuery(id+"F4.wireOp",EDGE,"E92.17"),sQuery(id+"F4.wireOp",EDGE,"E93"),sQuery(id+"F4.wireOp",EDGE,"E94")])],"isStart":false})]});
            var Q14;
            Q14=makeQuery(id+"F6.boolean.opBoolean","INTERSECT",EDGE,{"derivedFrom":[makeQuery(id+"F1.opExtrude","SWEPT_FACE",FACE,{"disambiguationData":[OSD([sQuery(id+"F0.wireOp",EDGE,"E86")])]}),makeQuery(id+"F5.opExtrude","CAP_FACE",FACE,{"disambiguationData":[OSD([sQuery(id+"F4.wireOp",EDGE,"E92.0"),sQuery(id+"F4.wireOp",EDGE,"E92.1"),sQuery(id+"F4.wireOp",EDGE,"E92.2"),sQuery(id+"F4.wireOp",EDGE,"E92.3"),sQuery(id+"F4.wireOp",EDGE,"E92.4"),sQuery(id+"F4.wireOp",EDGE,"E92.5"),sQuery(id+"F4.wireOp",EDGE,"E92.6"),sQuery(id+"F4.wireOp",EDGE,"E92.7"),sQuery(id+"F4.wireOp",EDGE,"E92.8"),sQuery(id+"F4.wireOp",EDGE,"E92.9"),sQuery(id+"F4.wireOp",EDGE,"E92.10"),sQuery(id+"F4.wireOp",EDGE,"E92.11"),sQuery(id+"F4.wireOp",EDGE,"E92.12"),sQuery(id+"F4.wireOp",EDGE,"E92.13"),sQuery(id+"F4.wireOp",EDGE,"E92.14"),sQuery(id+"F4.wireOp",EDGE,"E92.15"),sQuery(id+"F4.wireOp",EDGE,"E92.16"),sQuery(id+"F4.wireOp",EDGE,"E92.17"),sQuery(id+"F4.wireOp",EDGE,"E93"),sQuery(id+"F4.wireOp",EDGE,"E94")])],"isStart":false})]});
            var Q15;
            Q15=makeQuery(id+"F6.boolean.opBoolean","INTERSECT",EDGE,{"derivedFrom":[makeQuery(id+"F1.opExtrude","SWEPT_FACE",FACE,{"disambiguationData":[OSD([sQuery(id+"F0.wireOp",EDGE,"E84")])]}),makeQuery(id+"F5.opExtrude","CAP_FACE",FACE,{"disambiguationData":[OSD([sQuery(id+"F4.wireOp",EDGE,"E92.0"),sQuery(id+"F4.wireOp",EDGE,"E92.1"),sQuery(id+"F4.wireOp",EDGE,"E92.2"),sQuery(id+"F4.wireOp",EDGE,"E92.3"),sQuery(id+"F4.wireOp",EDGE,"E92.4"),sQuery(id+"F4.wireOp",EDGE,"E92.5"),sQuery(id+"F4.wireOp",EDGE,"E92.6"),sQuery(id+"F4.wireOp",EDGE,"E92.7"),sQuery(id+"F4.wireOp",EDGE,"E92.8"),sQuery(id+"F4.wireOp",EDGE,"E92.9"),sQuery(id+"F4.wireOp",EDGE,"E92.10"),sQuery(id+"F4.wireOp",EDGE,"E92.11"),sQuery(id+"F4.wireOp",EDGE,"E92.12"),sQuery(id+"F4.wireOp",EDGE,"E92.13"),sQuery(id+"F4.wireOp",EDGE,"E92.14"),sQuery(id+"F4.wireOp",EDGE,"E92.15"),sQuery(id+"F4.wireOp",EDGE,"E92.16"),sQuery(id+"F4.wireOp",EDGE,"E92.17"),sQuery(id+"F4.wireOp",EDGE,"E93"),sQuery(id+"F4.wireOp",EDGE,"E94")])],"isStart":false})]});
            var Q16;
            Q16=makeQuery(id+"F6.boolean.opBoolean","INTERSECT",EDGE,{"derivedFrom":[makeQuery(id+"F1.opExtrude","SWEPT_FACE",FACE,{"disambiguationData":[OSD([sQuery(id+"F0.wireOp",EDGE,"E66")])]}),makeQuery(id+"F5.opExtrude","CAP_FACE",FACE,{"disambiguationData":[OSD([sQuery(id+"F4.wireOp",EDGE,"E92.0"),sQuery(id+"F4.wireOp",EDGE,"E92.1"),sQuery(id+"F4.wireOp",EDGE,"E92.2"),sQuery(id+"F4.wireOp",EDGE,"E92.3"),sQuery(id+"F4.wireOp",EDGE,"E92.4"),sQuery(id+"F4.wireOp",EDGE,"E92.5"),sQuery(id+"F4.wireOp",EDGE,"E92.6"),sQuery(id+"F4.wireOp",EDGE,"E92.7"),sQuery(id+"F4.wireOp",EDGE,"E92.8"),sQuery(id+"F4.wireOp",EDGE,"E92.9"),sQuery(id+"F4.wireOp",EDGE,"E92.10"),sQuery(id+"F4.wireOp",EDGE,"E92.11"),sQuery(id+"F4.wireOp",EDGE,"E92.12"),sQuery(id+"F4.wireOp",EDGE,"E92.13"),sQuery(id+"F4.wireOp",EDGE,"E92.14"),sQuery(id+"F4.wireOp",EDGE,"E92.15"),sQuery(id+"F4.wireOp",EDGE,"E92.16"),sQuery(id+"F4.wireOp",EDGE,"E92.17"),sQuery(id+"F4.wireOp",EDGE,"E93"),sQuery(id+"F4.wireOp",EDGE,"E94")])],"isStart":false})]});
            var Q17;
            Q17=makeQuery(id+"F6.boolean.opBoolean","INTERSECT",EDGE,{"derivedFrom":[makeQuery(id+"F1.opExtrude","SWEPT_FACE",FACE,{"disambiguationData":[OSD([sQuery(id+"F0.wireOp",EDGE,"E79")])]}),makeQuery(id+"F5.opExtrude","CAP_FACE",FACE,{"disambiguationData":[OSD([sQuery(id+"F4.wireOp",EDGE,"E92.0"),sQuery(id+"F4.wireOp",EDGE,"E92.1"),sQuery(id+"F4.wireOp",EDGE,"E92.2"),sQuery(id+"F4.wireOp",EDGE,"E92.3"),sQuery(id+"F4.wireOp",EDGE,"E92.4"),sQuery(id+"F4.wireOp",EDGE,"E92.5"),sQuery(id+"F4.wireOp",EDGE,"E92.6"),sQuery(id+"F4.wireOp",EDGE,"E92.7"),sQuery(id+"F4.wireOp",EDGE,"E92.8"),sQuery(id+"F4.wireOp",EDGE,"E92.9"),sQuery(id+"F4.wireOp",EDGE,"E92.10"),sQuery(id+"F4.wireOp",EDGE,"E92.11"),sQuery(id+"F4.wireOp",EDGE,"E92.12"),sQuery(id+"F4.wireOp",EDGE,"E92.13"),sQuery(id+"F4.wireOp",EDGE,"E92.14"),sQuery(id+"F4.wireOp",EDGE,"E92.15"),sQuery(id+"F4.wireOp",EDGE,"E92.16"),sQuery(id+"F4.wireOp",EDGE,"E92.17"),sQuery(id+"F4.wireOp",EDGE,"E93"),sQuery(id+"F4.wireOp",EDGE,"E94")])],"isStart":false})]});
            var Q18;
            Q18=makeQuery(id+"F6.boolean.opBoolean","INTERSECT",EDGE,{"derivedFrom":[makeQuery(id+"F1.opExtrude","SWEPT_FACE",FACE,{"disambiguationData":[OSD([sQuery(id+"F0.wireOp",EDGE,"E64")])]}),makeQuery(id+"F5.opExtrude","CAP_FACE",FACE,{"disambiguationData":[OSD([sQuery(id+"F4.wireOp",EDGE,"E92.0"),sQuery(id+"F4.wireOp",EDGE,"E92.1"),sQuery(id+"F4.wireOp",EDGE,"E92.2"),sQuery(id+"F4.wireOp",EDGE,"E92.3"),sQuery(id+"F4.wireOp",EDGE,"E92.4"),sQuery(id+"F4.wireOp",EDGE,"E92.5"),sQuery(id+"F4.wireOp",EDGE,"E92.6"),sQuery(id+"F4.wireOp",EDGE,"E92.7"),sQuery(id+"F4.wireOp",EDGE,"E92.8"),sQuery(id+"F4.wireOp",EDGE,"E92.9"),sQuery(id+"F4.wireOp",EDGE,"E92.10"),sQuery(id+"F4.wireOp",EDGE,"E92.11"),sQuery(id+"F4.wireOp",EDGE,"E92.12"),sQuery(id+"F4.wireOp",EDGE,"E92.13"),sQuery(id+"F4.wireOp",EDGE,"E92.14"),sQuery(id+"F4.wireOp",EDGE,"E92.15"),sQuery(id+"F4.wireOp",EDGE,"E92.16"),sQuery(id+"F4.wireOp",EDGE,"E92.17"),sQuery(id+"F4.wireOp",EDGE,"E93"),sQuery(id+"F4.wireOp",EDGE,"E94")])],"isStart":false})]});
            var Q19;
            Q19=makeQuery(id+"F6.boolean.opBoolean","INTERSECT",EDGE,{"derivedFrom":[makeQuery(id+"F1.opExtrude","SWEPT_FACE",FACE,{"disambiguationData":[OSD([sQuery(id+"F0.wireOp",EDGE,"E61")])]}),makeQuery(id+"F5.opExtrude","CAP_FACE",FACE,{"disambiguationData":[OSD([sQuery(id+"F4.wireOp",EDGE,"E92.0"),sQuery(id+"F4.wireOp",EDGE,"E92.1"),sQuery(id+"F4.wireOp",EDGE,"E92.2"),sQuery(id+"F4.wireOp",EDGE,"E92.3"),sQuery(id+"F4.wireOp",EDGE,"E92.4"),sQuery(id+"F4.wireOp",EDGE,"E92.5"),sQuery(id+"F4.wireOp",EDGE,"E92.6"),sQuery(id+"F4.wireOp",EDGE,"E92.7"),sQuery(id+"F4.wireOp",EDGE,"E92.8"),sQuery(id+"F4.wireOp",EDGE,"E92.9"),sQuery(id+"F4.wireOp",EDGE,"E92.10"),sQuery(id+"F4.wireOp",EDGE,"E92.11"),sQuery(id+"F4.wireOp",EDGE,"E92.12"),sQuery(id+"F4.wireOp",EDGE,"E92.13"),sQuery(id+"F4.wireOp",EDGE,"E92.14"),sQuery(id+"F4.wireOp",EDGE,"E92.15"),sQuery(id+"F4.wireOp",EDGE,"E92.16"),sQuery(id+"F4.wireOp",EDGE,"E92.17"),sQuery(id+"F4.wireOp",EDGE,"E93"),sQuery(id+"F4.wireOp",EDGE,"E94")])],"isStart":false})]});
            fillet(context, id + "F13", {"entities" : qUnion([Q0, Q1, Q2, Q3, Q4, Q5, Q6, Q7, Q8, Q9, Q10, Q11, Q12, Q13, Q14, Q15, Q16, Q17, Q18, Q19]), "radius" : 7.62 * mm, "tangentPropagation" : true, "allowEdgeOverflow" : false});
        }
        {
            var Q0;
            Q0=makeQuery(id+"F1.opExtrude","SWEPT_BODY",BODY,{"disambiguationData":[OSD([sQuery(id+"F0.wireOp",EDGE,"E0"),sQuery(id+"F0.wireOp",EDGE,"E1"),sQuery(id+"F0.wireOp",EDGE,"E2"),sQuery(id+"F0.wireOp",EDGE,"E4"),sQuery(id+"F0.wireOp",EDGE,"E5"),sQuery(id+"F0.wireOp",EDGE,"E7"),sQuery(id+"F0.wireOp",EDGE,"E8"),sQuery(id+"F0.wireOp",EDGE,"E9"),sQuery(id+"F0.wireOp",EDGE,"E11"),sQuery(id+"F0.wireOp",EDGE,"E12"),sQuery(id+"F0.wireOp",EDGE,"E13"),sQuery(id+"F0.wireOp",EDGE,"E15"),sQuery(id+"F0.wireOp",EDGE,"E16"),sQuery(id+"F0.wireOp",EDGE,"E17"),sQuery(id+"F0.wireOp",EDGE,"E18"),sQuery(id+"F0.wireOp",EDGE,"E19"),sQuery(id+"F0.wireOp",EDGE,"E20"),sQuery(id+"F0.wireOp",EDGE,"E22"),sQuery(id+"F0.wireOp",EDGE,"E23"),sQuery(id+"F0.wireOp",EDGE,"E25"),sQuery(id+"F0.wireOp",EDGE,"E27"),sQuery(id+"F0.wireOp",EDGE,"E28"),sQuery(id+"F0.wireOp",EDGE,"E29"),sQuery(id+"F0.wireOp",EDGE,"E31"),sQuery(id+"F0.wireOp",EDGE,"E33"),sQuery(id+"F0.wireOp",EDGE,"E34"),sQuery(id+"F0.wireOp",EDGE,"E36"),sQuery(id+"F0.wireOp",EDGE,"E37"),sQuery(id+"F0.wireOp",EDGE,"E38"),sQuery(id+"F0.wireOp",EDGE,"E40"),sQuery(id+"F0.wireOp",EDGE,"E41"),sQuery(id+"F0.wireOp",EDGE,"E42"),sQuery(id+"F0.wireOp",EDGE,"E44"),sQuery(id+"F0.wireOp",EDGE,"E45"),sQuery(id+"F0.wireOp",EDGE,"E49"),sQuery(id+"F0.wireOp",EDGE,"E50"),sQuery(id+"F0.wireOp",EDGE,"E51"),sQuery(id+"F0.wireOp",EDGE,"E53"),sQuery(id+"F0.wireOp",EDGE,"E54"),sQuery(id+"F0.wireOp",EDGE,"E55"),sQuery(id+"F0.wireOp",EDGE,"E57"),sQuery(id+"F0.wireOp",EDGE,"E58"),sQuery(id+"F0.wireOp",EDGE,"E59"),sQuery(id+"F0.wireOp",EDGE,"E60"),sQuery(id+"F0.wireOp",EDGE,"E61"),sQuery(id+"F0.wireOp",EDGE,"E62"),sQuery(id+"F0.wireOp",EDGE,"E63"),sQuery(id+"F0.wireOp",EDGE,"E64"),sQuery(id+"F0.wireOp",EDGE,"E65"),sQuery(id+"F0.wireOp",EDGE,"E66"),sQuery(id+"F0.wireOp",EDGE,"E67"),sQuery(id+"F0.wireOp",EDGE,"E68"),sQuery(id+"F0.wireOp",EDGE,"E69"),sQuery(id+"F0.wireOp",EDGE,"E70"),sQuery(id+"F0.wireOp",EDGE,"E71"),sQuery(id+"F0.wireOp",EDGE,"E72"),sQuery(id+"F0.wireOp",EDGE,"E73"),sQuery(id+"F0.wireOp",EDGE,"E74"),sQuery(id+"F0.wireOp",EDGE,"E75"),sQuery(id+"F0.wireOp",EDGE,"E78"),sQuery(id+"F0.wireOp",EDGE,"E79"),sQuery(id+"F0.wireOp",EDGE,"E80"),sQuery(id+"F0.wireOp",EDGE,"E81"),sQuery(id+"F0.wireOp",EDGE,"E82"),sQuery(id+"F0.wireOp",EDGE,"E83"),sQuery(id+"F0.wireOp",EDGE,"E84"),sQuery(id+"F0.wireOp",EDGE,"E85"),sQuery(id+"F0.wireOp",EDGE,"E86"),sQuery(id+"F0.wireOp",EDGE,"E87"),sQuery(id+"F0.wireOp",EDGE,"E88"),sQuery(id+"F0.wireOp",EDGE,"E89"),sQuery(id+"F0.wireOp",EDGE,"E90"),sQuery(id+"F0.wireOp",EDGE,"E91")])]});
            transform(context, id + "F14", {"entities" : qUnion([Q0]), "transformType" : TransformType.COPY});
        }
        {
            var Q0;
            Q0=makeQuery(id+"F14.opPattern","COPY",BODY,{"derivedFrom":makeQuery(id+"F1.opExtrude","SWEPT_BODY",BODY,{"disambiguationData":[OSD([sQuery(id+"F0.wireOp",EDGE,"E0"),sQuery(id+"F0.wireOp",EDGE,"E1"),sQuery(id+"F0.wireOp",EDGE,"E2"),sQuery(id+"F0.wireOp",EDGE,"E4"),sQuery(id+"F0.wireOp",EDGE,"E5"),sQuery(id+"F0.wireOp",EDGE,"E7"),sQuery(id+"F0.wireOp",EDGE,"E8"),sQuery(id+"F0.wireOp",EDGE,"E9"),sQuery(id+"F0.wireOp",EDGE,"E11"),sQuery(id+"F0.wireOp",EDGE,"E12"),sQuery(id+"F0.wireOp",EDGE,"E13"),sQuery(id+"F0.wireOp",EDGE,"E15"),sQuery(id+"F0.wireOp",EDGE,"E16"),sQuery(id+"F0.wireOp",EDGE,"E17"),sQuery(id+"F0.wireOp",EDGE,"E18"),sQuery(id+"F0.wireOp",EDGE,"E19"),sQuery(id+"F0.wireOp",EDGE,"E20"),sQuery(id+"F0.wireOp",EDGE,"E22"),sQuery(id+"F0.wireOp",EDGE,"E23"),sQuery(id+"F0.wireOp",EDGE,"E25"),sQuery(id+"F0.wireOp",EDGE,"E27"),sQuery(id+"F0.wireOp",EDGE,"E28"),sQuery(id+"F0.wireOp",EDGE,"E29"),sQuery(id+"F0.wireOp",EDGE,"E31"),sQuery(id+"F0.wireOp",EDGE,"E33"),sQuery(id+"F0.wireOp",EDGE,"E34"),sQuery(id+"F0.wireOp",EDGE,"E36"),sQuery(id+"F0.wireOp",EDGE,"E37"),sQuery(id+"F0.wireOp",EDGE,"E38"),sQuery(id+"F0.wireOp",EDGE,"E40"),sQuery(id+"F0.wireOp",EDGE,"E41"),sQuery(id+"F0.wireOp",EDGE,"E42"),sQuery(id+"F0.wireOp",EDGE,"E44"),sQuery(id+"F0.wireOp",EDGE,"E45"),sQuery(id+"F0.wireOp",EDGE,"E49"),sQuery(id+"F0.wireOp",EDGE,"E50"),sQuery(id+"F0.wireOp",EDGE,"E51"),sQuery(id+"F0.wireOp",EDGE,"E53"),sQuery(id+"F0.wireOp",EDGE,"E54"),sQuery(id+"F0.wireOp",EDGE,"E55"),sQuery(id+"F0.wireOp",EDGE,"E57"),sQuery(id+"F0.wireOp",EDGE,"E58"),sQuery(id+"F0.wireOp",EDGE,"E59"),sQuery(id+"F0.wireOp",EDGE,"E60"),sQuery(id+"F0.wireOp",EDGE,"E61"),sQuery(id+"F0.wireOp",EDGE,"E62"),sQuery(id+"F0.wireOp",EDGE,"E63"),sQuery(id+"F0.wireOp",EDGE,"E64"),sQuery(id+"F0.wireOp",EDGE,"E65"),sQuery(id+"F0.wireOp",EDGE,"E66"),sQuery(id+"F0.wireOp",EDGE,"E67"),sQuery(id+"F0.wireOp",EDGE,"E68"),sQuery(id+"F0.wireOp",EDGE,"E69"),sQuery(id+"F0.wireOp",EDGE,"E70"),sQuery(id+"F0.wireOp",EDGE,"E71"),sQuery(id+"F0.wireOp",EDGE,"E72"),sQuery(id+"F0.wireOp",EDGE,"E73"),sQuery(id+"F0.wireOp",EDGE,"E74"),sQuery(id+"F0.wireOp",EDGE,"E75"),sQuery(id+"F0.wireOp",EDGE,"E78"),sQuery(id+"F0.wireOp",EDGE,"E79"),sQuery(id+"F0.wireOp",EDGE,"E80"),sQuery(id+"F0.wireOp",EDGE,"E81"),sQuery(id+"F0.wireOp",EDGE,"E82"),sQuery(id+"F0.wireOp",EDGE,"E83"),sQuery(id+"F0.wireOp",EDGE,"E84"),sQuery(id+"F0.wireOp",EDGE,"E85"),sQuery(id+"F0.wireOp",EDGE,"E86"),sQuery(id+"F0.wireOp",EDGE,"E87"),sQuery(id+"F0.wireOp",EDGE,"E88"),sQuery(id+"F0.wireOp",EDGE,"E89"),sQuery(id+"F0.wireOp",EDGE,"E90"),sQuery(id+"F0.wireOp",EDGE,"E91")])]}),"instanceName":"1"});
            transform(context, id + "F15", {"entities" : qUnion([Q0]), "transformType" : TransformType.TRANSLATION_3D, "dx" : 0 * mm, "dy" : 314.96 * mm, "dz" : 0 * mm, "makeCopy" : false});
        }
    });
